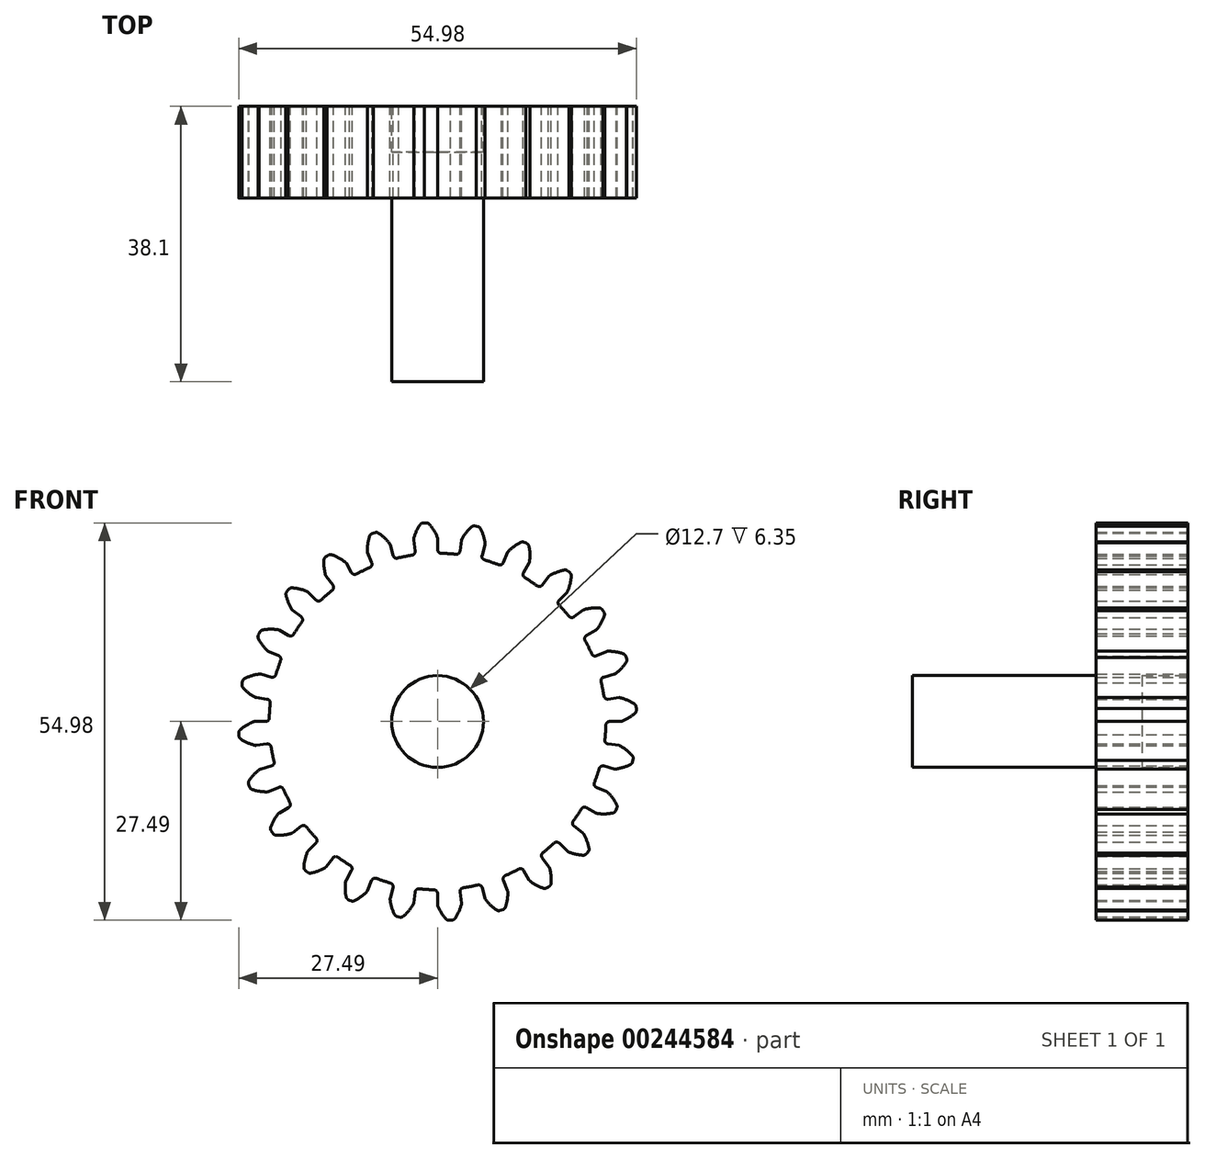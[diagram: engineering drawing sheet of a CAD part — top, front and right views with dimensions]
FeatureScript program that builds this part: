
annotation { "Feature Type Name" : "Feature", "Feature Type Description" : "" }
export const myFeature = defineFeature(function(context is Context, id is Id, definition is map)
    precondition{}
    {
        {
            var Q0;
            Q0=qCreatedBy(makeId("Front.planeOp"),FACE);
            var sketch = newSketch(context, id + "F0", { "sketchPlane" : qUnion([Q0])});
            skArc(sketch, "E0", {"start": v(-3.53, 23) * mm, "mid": v(-4.54, 22.83) * mm, "end": v(-5.54, 22.6) * mm});
            skArc(sketch, "E1.trimOffspring", {"start": v(-0.04, 25.5) * mm, "mid": v(-0.52, 26.45) * mm, "end": v(-1.16, 27.32) * mm});
            skLineSegment(sketch, "E2", {"start": v(0, 25.4) * mm, "end": v(0, 23.78) * mm});
            skLineSegment(sketch, "E3", {"start": v(-1.54, 27.49) * mm, "end": v(-1.8, 27.49) * mm});
            skLineSegment(sketch, "E4", {"start": v(0, 25.3) * mm, "end": v(0, 23.78) * mm});
            skArc(sketch, "E5.MirrorCS", {"start": v(-3.3, 25.28) * mm, "mid": v(-2.94, 26.3) * mm, "end": v(-2.41, 27.23) * mm});
            skLineSegment(sketch, "E6.MirrorCS", {"start": v(-2.06, 27.46) * mm, "end": v(-1.8, 27.49) * mm});
            skLineSegment(sketch, "E7.MirrorCS", {"start": v(-3.3, 25.09) * mm, "end": v(-3.1, 23.58) * mm});
            skPoint(sketch, "E8.visualSharp", {"position": v(-3.04, 23.08) * mm});
            skArc(sketch, "E8.filletArc", {"start": v(-3.53, 23) * mm, "mid": v(-3.2, 23.2) * mm, "end": v(-3.1, 23.58) * mm});
            skPoint(sketch, "E9.visualSharp", {"position": v(0, 23.28) * mm});
            skArc(sketch, "E9.filletArc", {"start": v(0, 23.78) * mm, "mid": v(0.14, 23.43) * mm, "end": v(0.5, 23.27) * mm});
            skPoint(sketch, "E10.visualSharp", {"position": v(0, 25.4) * mm});
            skArc(sketch, "E10.filletArc", {"start": v(0, 25.3) * mm, "mid": v(0, 25.4) * mm, "end": v(-0.04, 25.5) * mm});
            skPoint(sketch, "E11.visualSharp", {"position": v(-3.32, 25.18) * mm});
            skArc(sketch, "E11.filletArc", {"start": v(-3.3, 25.28) * mm, "mid": v(-3.3, 25.18) * mm, "end": v(-3.3, 25.09) * mm});
            skPoint(sketch, "E12.visualSharp", {"position": v(-2.28, 27.43) * mm});
            skArc(sketch, "E12.filletArc", {"start": v(-2.06, 27.46) * mm, "mid": v(-2.26, 27.38) * mm, "end": v(-2.41, 27.23) * mm});
            skPoint(sketch, "E13.visualSharp", {"position": v(-1.32, 27.49) * mm});
            skArc(sketch, "E13.filletArc", {"start": v(-1.16, 27.32) * mm, "mid": v(-1.33, 27.44) * mm, "end": v(-1.54, 27.49) * mm});
            skArc(sketch, "E14.1.0", {"start": v(-9.37, 21.31) * mm, "mid": v(-9.1, 21.59) * mm, "end": v(-9.1, 21.97) * mm});
            skLineSegment(sketch, "E14.1.1", {"start": v(-9.68, 23.38) * mm, "end": v(-9.1, 21.97) * mm});
            skArc(sketch, "E14.1.2", {"start": v(-9.72, 23.57) * mm, "mid": v(-9.71, 23.47) * mm, "end": v(-9.68, 23.38) * mm});
            skArc(sketch, "E14.1.3", {"start": v(-6.55, 24.44) * mm, "mid": v(-6.58, 24.53) * mm, "end": v(-6.63, 24.62) * mm});
            skLineSegment(sketch, "E14.1.4", {"start": v(-6.55, 24.44) * mm, "end": v(-6.16, 22.97) * mm});
            skArc(sketch, "E14.1.5", {"start": v(-6.16, 22.97) * mm, "mid": v(-5.92, 22.67) * mm, "end": v(-5.54, 22.6) * mm});
            skArc(sketch, "E14.1.6", {"start": v(-6.63, 24.62) * mm, "mid": v(-7.35, 25.42) * mm, "end": v(-8.2, 26.09) * mm});
            skArc(sketch, "E14.1.7", {"start": v(-9.72, 23.57) * mm, "mid": v(-9.64, 24.64) * mm, "end": v(-9.38, 25.68) * mm});
            skArc(sketch, "E14.1.8", {"start": v(-9.1, 25.99) * mm, "mid": v(-9.27, 25.87) * mm, "end": v(-9.38, 25.68) * mm});
            skLineSegment(sketch, "E14.1.9", {"start": v(-9.1, 25.99) * mm, "end": v(-8.86, 26.09) * mm});
            skLineSegment(sketch, "E14.1.10", {"start": v(-8.6, 26.15) * mm, "end": v(-8.86, 26.09) * mm});
            skArc(sketch, "E14.1.11", {"start": v(-8.2, 26.09) * mm, "mid": v(-8.4, 26.16) * mm, "end": v(-8.6, 26.15) * mm});
            skArc(sketch, "E14.2.0", {"start": v(-14.56, 18.16) * mm, "mid": v(-14.38, 18.5) * mm, "end": v(-14.48, 18.87) * mm});
            skLineSegment(sketch, "E14.2.1", {"start": v(-15.4, 20.07) * mm, "end": v(-14.48, 18.87) * mm});
            skArc(sketch, "E14.2.2", {"start": v(-15.5, 20.25) * mm, "mid": v(-15.46, 20.16) * mm, "end": v(-15.4, 20.07) * mm});
            skArc(sketch, "E14.2.3", {"start": v(-12.65, 21.91) * mm, "mid": v(-12.7, 22) * mm, "end": v(-12.78, 22.06) * mm});
            skLineSegment(sketch, "E14.2.4", {"start": v(-12.65, 21.91) * mm, "end": v(-11.9, 20.6) * mm});
            skArc(sketch, "E14.2.5", {"start": v(-11.9, 20.6) * mm, "mid": v(-11.59, 20.36) * mm, "end": v(-11.2, 20.4) * mm});
            skArc(sketch, "E14.2.6", {"start": v(-12.78, 22.06) * mm, "mid": v(-13.68, 22.65) * mm, "end": v(-14.66, 23.08) * mm});
            skArc(sketch, "E14.2.7", {"start": v(-15.5, 20.25) * mm, "mid": v(-15.69, 21.3) * mm, "end": v(-15.7, 22.38) * mm});
            skArc(sketch, "E14.2.8", {"start": v(-15.51, 22.75) * mm, "mid": v(-15.65, 22.58) * mm, "end": v(-15.7, 22.38) * mm});
            skLineSegment(sketch, "E14.2.9", {"start": v(-15.51, 22.75) * mm, "end": v(-15.3, 22.9) * mm});
            skLineSegment(sketch, "E14.2.10", {"start": v(-15.08, 23.04) * mm, "end": v(-15.3, 22.9) * mm});
            skArc(sketch, "E14.2.11", {"start": v(-14.66, 23.08) * mm, "mid": v(-14.88, 23.1) * mm, "end": v(-15.08, 23.04) * mm});
            skArc(sketch, "E14.3.0", {"start": v(-18.77, 13.77) * mm, "mid": v(-18.67, 14.15) * mm, "end": v(-18.87, 14.48) * mm});
            skLineSegment(sketch, "E14.3.1", {"start": v(-20.07, 15.4) * mm, "end": v(-18.87, 14.48) * mm});
            skArc(sketch, "E14.3.2", {"start": v(-20.2, 15.55) * mm, "mid": v(-20.15, 15.47) * mm, "end": v(-20.07, 15.4) * mm});
            skArc(sketch, "E14.3.3", {"start": v(-17.9, 17.9) * mm, "mid": v(-17.97, 17.95) * mm, "end": v(-18.05, 18) * mm});
            skLineSegment(sketch, "E14.3.4", {"start": v(-17.9, 17.9) * mm, "end": v(-16.82, 16.82) * mm});
            skArc(sketch, "E14.3.5", {"start": v(-16.82, 16.82) * mm, "mid": v(-16.46, 16.67) * mm, "end": v(-16.1, 16.8) * mm});
            skArc(sketch, "E14.3.6", {"start": v(-18.05, 18) * mm, "mid": v(-19.07, 18.34) * mm, "end": v(-20.14, 18.5) * mm});
            skArc(sketch, "E14.3.7", {"start": v(-20.2, 15.55) * mm, "mid": v(-20.67, 16.52) * mm, "end": v(-20.97, 17.55) * mm});
            skArc(sketch, "E14.3.8", {"start": v(-20.87, 17.96) * mm, "mid": v(-20.96, 17.76) * mm, "end": v(-20.97, 17.55) * mm});
            skLineSegment(sketch, "E14.3.9", {"start": v(-20.87, 17.96) * mm, "end": v(-20.71, 18.16) * mm});
            skLineSegment(sketch, "E14.3.10", {"start": v(-20.53, 18.35) * mm, "end": v(-20.71, 18.16) * mm});
            skArc(sketch, "E14.3.11", {"start": v(-20.14, 18.5) * mm, "mid": v(-20.35, 18.46) * mm, "end": v(-20.53, 18.35) * mm});
            skArc(sketch, "E14.4.0", {"start": v(-21.7, 8.45) * mm, "mid": v(-21.7, 8.83) * mm, "end": v(-21.97, 9.1) * mm});
            skLineSegment(sketch, "E14.4.1", {"start": v(-23.38, 9.68) * mm, "end": v(-21.97, 9.1) * mm});
            skArc(sketch, "E14.4.2", {"start": v(-23.54, 9.79) * mm, "mid": v(-23.46, 9.73) * mm, "end": v(-23.38, 9.68) * mm});
            skArc(sketch, "E14.4.3", {"start": v(-21.91, 12.65) * mm, "mid": v(-22, 12.7) * mm, "end": v(-22.1, 12.71) * mm});
            skLineSegment(sketch, "E14.4.4", {"start": v(-21.91, 12.65) * mm, "end": v(-20.6, 11.9) * mm});
            skArc(sketch, "E14.4.5", {"start": v(-20.6, 11.9) * mm, "mid": v(-20.22, 11.84) * mm, "end": v(-19.9, 12.07) * mm});
            skArc(sketch, "E14.4.6", {"start": v(-22.1, 12.71) * mm, "mid": v(-23.17, 12.77) * mm, "end": v(-24.24, 12.65) * mm});
            skArc(sketch, "E14.4.7", {"start": v(-23.54, 9.79) * mm, "mid": v(-24.24, 10.6) * mm, "end": v(-24.8, 11.53) * mm});
            skArc(sketch, "E14.4.8", {"start": v(-24.8, 11.94) * mm, "mid": v(-24.85, 11.73) * mm, "end": v(-24.8, 11.53) * mm});
            skLineSegment(sketch, "E14.4.9", {"start": v(-24.8, 11.94) * mm, "end": v(-24.7, 12.18) * mm});
            skLineSegment(sketch, "E14.4.10", {"start": v(-24.58, 12.4) * mm, "end": v(-24.7, 12.18) * mm});
            skArc(sketch, "E14.4.11", {"start": v(-24.24, 12.65) * mm, "mid": v(-24.43, 12.57) * mm, "end": v(-24.58, 12.4) * mm});
            skArc(sketch, "E14.5.0", {"start": v(-23.14, 2.54) * mm, "mid": v(-23.24, 2.91) * mm, "end": v(-23.58, 3.1) * mm});
            skLineSegment(sketch, "E14.5.1", {"start": v(-25.09, 3.3) * mm, "end": v(-23.58, 3.1) * mm});
            skArc(sketch, "E14.5.2", {"start": v(-25.27, 3.36) * mm, "mid": v(-25.18, 3.32) * mm, "end": v(-25.09, 3.3) * mm});
            skArc(sketch, "E14.5.3", {"start": v(-24.44, 6.55) * mm, "mid": v(-24.54, 6.57) * mm, "end": v(-24.63, 6.56) * mm});
            skLineSegment(sketch, "E14.5.4", {"start": v(-24.44, 6.55) * mm, "end": v(-22.97, 6.16) * mm});
            skArc(sketch, "E14.5.5", {"start": v(-22.97, 6.16) * mm, "mid": v(-22.6, 6.2) * mm, "end": v(-22.35, 6.5) * mm});
            skArc(sketch, "E14.5.6", {"start": v(-24.63, 6.56) * mm, "mid": v(-25.69, 6.34) * mm, "end": v(-26.69, 5.95) * mm});
            skArc(sketch, "E14.5.7", {"start": v(-25.27, 3.36) * mm, "mid": v(-26.16, 3.97) * mm, "end": v(-26.93, 4.72) * mm});
            skArc(sketch, "E14.5.8", {"start": v(-27.05, 5.12) * mm, "mid": v(-27.04, 4.9) * mm, "end": v(-26.93, 4.72) * mm});
            skLineSegment(sketch, "E14.5.9", {"start": v(-27.05, 5.12) * mm, "end": v(-27.02, 5.37) * mm});
            skLineSegment(sketch, "E14.5.10", {"start": v(-26.95, 5.63) * mm, "end": v(-27.02, 5.37) * mm});
            skArc(sketch, "E14.5.11", {"start": v(-26.69, 5.95) * mm, "mid": v(-26.85, 5.82) * mm, "end": v(-26.95, 5.63) * mm});
            skArc(sketch, "E14.6.0", {"start": v(-23, -3.53) * mm, "mid": v(-23.2, -3.2) * mm, "end": v(-23.58, -3.1) * mm});
            skLineSegment(sketch, "E14.6.1", {"start": v(-25.09, -3.3) * mm, "end": v(-23.58, -3.1) * mm});
            skArc(sketch, "E14.6.2", {"start": v(-25.28, -3.3) * mm, "mid": v(-25.18, -3.3) * mm, "end": v(-25.09, -3.3) * mm});
            skArc(sketch, "E14.6.3", {"start": v(-25.3, 0) * mm, "mid": v(-25.4, 0) * mm, "end": v(-25.5, -0.04) * mm});
            skLineSegment(sketch, "E14.6.4", {"start": v(-25.3, 0) * mm, "end": v(-23.78, 0) * mm});
            skArc(sketch, "E14.6.5", {"start": v(-23.78, 0) * mm, "mid": v(-23.43, 0.14) * mm, "end": v(-23.27, 0.5) * mm});
            skArc(sketch, "E14.6.6", {"start": v(-25.5, -0.04) * mm, "mid": v(-26.45, -0.52) * mm, "end": v(-27.32, -1.16) * mm});
            skArc(sketch, "E14.6.7", {"start": v(-25.28, -3.3) * mm, "mid": v(-26.3, -2.94) * mm, "end": v(-27.23, -2.41) * mm});
            skArc(sketch, "E14.6.8", {"start": v(-27.46, -2.06) * mm, "mid": v(-27.38, -2.26) * mm, "end": v(-27.23, -2.41) * mm});
            skLineSegment(sketch, "E14.6.9", {"start": v(-27.46, -2.06) * mm, "end": v(-27.49, -1.8) * mm});
            skLineSegment(sketch, "E14.6.10", {"start": v(-27.49, -1.54) * mm, "end": v(-27.49, -1.8) * mm});
            skArc(sketch, "E14.6.11", {"start": v(-27.32, -1.16) * mm, "mid": v(-27.44, -1.33) * mm, "end": v(-27.49, -1.54) * mm});
            skArc(sketch, "E14.7.0", {"start": v(-21.31, -9.37) * mm, "mid": v(-21.59, -9.1) * mm, "end": v(-21.97, -9.1) * mm});
            skLineSegment(sketch, "E14.7.1", {"start": v(-23.38, -9.68) * mm, "end": v(-21.97, -9.1) * mm});
            skArc(sketch, "E14.7.2", {"start": v(-23.57, -9.72) * mm, "mid": v(-23.47, -9.71) * mm, "end": v(-23.38, -9.68) * mm});
            skArc(sketch, "E14.7.3", {"start": v(-24.44, -6.55) * mm, "mid": v(-24.53, -6.58) * mm, "end": v(-24.62, -6.63) * mm});
            skLineSegment(sketch, "E14.7.4", {"start": v(-24.44, -6.55) * mm, "end": v(-22.97, -6.16) * mm});
            skArc(sketch, "E14.7.5", {"start": v(-22.97, -6.16) * mm, "mid": v(-22.67, -5.92) * mm, "end": v(-22.6, -5.54) * mm});
            skArc(sketch, "E14.7.6", {"start": v(-24.62, -6.63) * mm, "mid": v(-25.42, -7.35) * mm, "end": v(-26.09, -8.2) * mm});
            skArc(sketch, "E14.7.7", {"start": v(-23.57, -9.72) * mm, "mid": v(-24.64, -9.64) * mm, "end": v(-25.68, -9.38) * mm});
            skArc(sketch, "E14.7.8", {"start": v(-25.99, -9.1) * mm, "mid": v(-25.87, -9.27) * mm, "end": v(-25.68, -9.38) * mm});
            skLineSegment(sketch, "E14.7.9", {"start": v(-25.99, -9.1) * mm, "end": v(-26.09, -8.86) * mm});
            skLineSegment(sketch, "E14.7.10", {"start": v(-26.15, -8.6) * mm, "end": v(-26.09, -8.86) * mm});
            skArc(sketch, "E14.7.11", {"start": v(-26.09, -8.2) * mm, "mid": v(-26.16, -8.4) * mm, "end": v(-26.15, -8.6) * mm});
            skArc(sketch, "E14.8.0", {"start": v(-18.16, -14.56) * mm, "mid": v(-18.5, -14.38) * mm, "end": v(-18.87, -14.48) * mm});
            skLineSegment(sketch, "E14.8.1", {"start": v(-20.07, -15.4) * mm, "end": v(-18.87, -14.48) * mm});
            skArc(sketch, "E14.8.2", {"start": v(-20.25, -15.5) * mm, "mid": v(-20.16, -15.46) * mm, "end": v(-20.07, -15.4) * mm});
            skArc(sketch, "E14.8.3", {"start": v(-21.91, -12.65) * mm, "mid": v(-22, -12.7) * mm, "end": v(-22.06, -12.78) * mm});
            skLineSegment(sketch, "E14.8.4", {"start": v(-21.91, -12.65) * mm, "end": v(-20.6, -11.9) * mm});
            skArc(sketch, "E14.8.5", {"start": v(-20.6, -11.9) * mm, "mid": v(-20.36, -11.59) * mm, "end": v(-20.4, -11.2) * mm});
            skArc(sketch, "E14.8.6", {"start": v(-22.06, -12.78) * mm, "mid": v(-22.65, -13.68) * mm, "end": v(-23.08, -14.66) * mm});
            skArc(sketch, "E14.8.7", {"start": v(-20.25, -15.5) * mm, "mid": v(-21.3, -15.69) * mm, "end": v(-22.38, -15.7) * mm});
            skArc(sketch, "E14.8.8", {"start": v(-22.75, -15.51) * mm, "mid": v(-22.58, -15.65) * mm, "end": v(-22.38, -15.7) * mm});
            skLineSegment(sketch, "E14.8.9", {"start": v(-22.75, -15.51) * mm, "end": v(-22.9, -15.3) * mm});
            skLineSegment(sketch, "E14.8.10", {"start": v(-23.04, -15.08) * mm, "end": v(-22.9, -15.3) * mm});
            skArc(sketch, "E14.8.11", {"start": v(-23.08, -14.66) * mm, "mid": v(-23.1, -14.88) * mm, "end": v(-23.04, -15.08) * mm});
            skArc(sketch, "E14.9.0", {"start": v(-13.77, -18.77) * mm, "mid": v(-14.15, -18.67) * mm, "end": v(-14.48, -18.87) * mm});
            skLineSegment(sketch, "E14.9.1", {"start": v(-15.4, -20.07) * mm, "end": v(-14.48, -18.87) * mm});
            skArc(sketch, "E14.9.2", {"start": v(-15.55, -20.2) * mm, "mid": v(-15.47, -20.15) * mm, "end": v(-15.4, -20.07) * mm});
            skArc(sketch, "E14.9.3", {"start": v(-17.9, -17.9) * mm, "mid": v(-17.95, -17.97) * mm, "end": v(-18, -18.05) * mm});
            skLineSegment(sketch, "E14.9.4", {"start": v(-17.9, -17.9) * mm, "end": v(-16.82, -16.82) * mm});
            skArc(sketch, "E14.9.5", {"start": v(-16.82, -16.82) * mm, "mid": v(-16.67, -16.46) * mm, "end": v(-16.8, -16.1) * mm});
            skArc(sketch, "E14.9.6", {"start": v(-18, -18.05) * mm, "mid": v(-18.34, -19.07) * mm, "end": v(-18.5, -20.14) * mm});
            skArc(sketch, "E14.9.7", {"start": v(-15.55, -20.2) * mm, "mid": v(-16.52, -20.67) * mm, "end": v(-17.55, -20.97) * mm});
            skArc(sketch, "E14.9.8", {"start": v(-17.96, -20.87) * mm, "mid": v(-17.76, -20.96) * mm, "end": v(-17.55, -20.97) * mm});
            skLineSegment(sketch, "E14.9.9", {"start": v(-17.96, -20.87) * mm, "end": v(-18.16, -20.71) * mm});
            skLineSegment(sketch, "E14.9.10", {"start": v(-18.35, -20.53) * mm, "end": v(-18.16, -20.71) * mm});
            skArc(sketch, "E14.9.11", {"start": v(-18.5, -20.14) * mm, "mid": v(-18.46, -20.35) * mm, "end": v(-18.35, -20.53) * mm});
            skArc(sketch, "E14.10.0", {"start": v(-8.45, -21.7) * mm, "mid": v(-8.83, -21.7) * mm, "end": v(-9.1, -21.97) * mm});
            skLineSegment(sketch, "E14.10.1", {"start": v(-9.68, -23.38) * mm, "end": v(-9.1, -21.97) * mm});
            skArc(sketch, "E14.10.2", {"start": v(-9.79, -23.54) * mm, "mid": v(-9.73, -23.46) * mm, "end": v(-9.68, -23.38) * mm});
            skArc(sketch, "E14.10.3", {"start": v(-12.65, -21.91) * mm, "mid": v(-12.7, -22) * mm, "end": v(-12.71, -22.1) * mm});
            skLineSegment(sketch, "E14.10.4", {"start": v(-12.65, -21.91) * mm, "end": v(-11.9, -20.6) * mm});
            skArc(sketch, "E14.10.5", {"start": v(-11.9, -20.6) * mm, "mid": v(-11.84, -20.22) * mm, "end": v(-12.07, -19.9) * mm});
            skArc(sketch, "E14.10.6", {"start": v(-12.71, -22.1) * mm, "mid": v(-12.77, -23.17) * mm, "end": v(-12.65, -24.24) * mm});
            skArc(sketch, "E14.10.7", {"start": v(-9.79, -23.54) * mm, "mid": v(-10.6, -24.24) * mm, "end": v(-11.53, -24.8) * mm});
            skArc(sketch, "E14.10.8", {"start": v(-11.94, -24.8) * mm, "mid": v(-11.73, -24.85) * mm, "end": v(-11.53, -24.8) * mm});
            skLineSegment(sketch, "E14.10.9", {"start": v(-11.94, -24.8) * mm, "end": v(-12.18, -24.7) * mm});
            skLineSegment(sketch, "E14.10.10", {"start": v(-12.4, -24.58) * mm, "end": v(-12.18, -24.7) * mm});
            skArc(sketch, "E14.10.11", {"start": v(-12.65, -24.24) * mm, "mid": v(-12.57, -24.43) * mm, "end": v(-12.4, -24.58) * mm});
            skArc(sketch, "E14.11.0", {"start": v(-2.54, -23.14) * mm, "mid": v(-2.91, -23.24) * mm, "end": v(-3.1, -23.58) * mm});
            skLineSegment(sketch, "E14.11.1", {"start": v(-3.3, -25.09) * mm, "end": v(-3.1, -23.58) * mm});
            skArc(sketch, "E14.11.2", {"start": v(-3.36, -25.27) * mm, "mid": v(-3.32, -25.18) * mm, "end": v(-3.3, -25.09) * mm});
            skArc(sketch, "E14.11.3", {"start": v(-6.55, -24.44) * mm, "mid": v(-6.57, -24.54) * mm, "end": v(-6.56, -24.63) * mm});
            skLineSegment(sketch, "E14.11.4", {"start": v(-6.55, -24.44) * mm, "end": v(-6.16, -22.97) * mm});
            skArc(sketch, "E14.11.5", {"start": v(-6.16, -22.97) * mm, "mid": v(-6.2, -22.6) * mm, "end": v(-6.5, -22.35) * mm});
            skArc(sketch, "E14.11.6", {"start": v(-6.56, -24.63) * mm, "mid": v(-6.34, -25.69) * mm, "end": v(-5.95, -26.69) * mm});
            skArc(sketch, "E14.11.7", {"start": v(-3.36, -25.27) * mm, "mid": v(-3.97, -26.16) * mm, "end": v(-4.72, -26.93) * mm});
            skArc(sketch, "E14.11.8", {"start": v(-5.12, -27.05) * mm, "mid": v(-4.9, -27.04) * mm, "end": v(-4.72, -26.93) * mm});
            skLineSegment(sketch, "E14.11.9", {"start": v(-5.12, -27.05) * mm, "end": v(-5.37, -27.02) * mm});
            skLineSegment(sketch, "E14.11.10", {"start": v(-5.63, -26.95) * mm, "end": v(-5.37, -27.02) * mm});
            skArc(sketch, "E14.11.11", {"start": v(-5.95, -26.69) * mm, "mid": v(-5.82, -26.85) * mm, "end": v(-5.63, -26.95) * mm});
            skArc(sketch, "E14.12.0", {"start": v(3.53, -23) * mm, "mid": v(3.2, -23.2) * mm, "end": v(3.1, -23.58) * mm});
            skLineSegment(sketch, "E14.12.1", {"start": v(3.3, -25.09) * mm, "end": v(3.1, -23.58) * mm});
            skArc(sketch, "E14.12.2", {"start": v(3.3, -25.28) * mm, "mid": v(3.3, -25.18) * mm, "end": v(3.3, -25.09) * mm});
            skArc(sketch, "E14.12.3", {"start": v(0, -25.3) * mm, "mid": v(0, -25.4) * mm, "end": v(0.04, -25.5) * mm});
            skLineSegment(sketch, "E14.12.4", {"start": v(0, -25.3) * mm, "end": v(0, -23.78) * mm});
            skArc(sketch, "E14.12.5", {"start": v(0, -23.78) * mm, "mid": v(-0.14, -23.43) * mm, "end": v(-0.5, -23.27) * mm});
            skArc(sketch, "E14.12.6", {"start": v(0.04, -25.5) * mm, "mid": v(0.52, -26.45) * mm, "end": v(1.16, -27.32) * mm});
            skArc(sketch, "E14.12.7", {"start": v(3.3, -25.28) * mm, "mid": v(2.94, -26.3) * mm, "end": v(2.41, -27.23) * mm});
            skArc(sketch, "E14.12.8", {"start": v(2.06, -27.46) * mm, "mid": v(2.26, -27.38) * mm, "end": v(2.41, -27.23) * mm});
            skLineSegment(sketch, "E14.12.9", {"start": v(2.06, -27.46) * mm, "end": v(1.8, -27.49) * mm});
            skLineSegment(sketch, "E14.12.10", {"start": v(1.54, -27.49) * mm, "end": v(1.8, -27.49) * mm});
            skArc(sketch, "E14.12.11", {"start": v(1.16, -27.32) * mm, "mid": v(1.33, -27.44) * mm, "end": v(1.54, -27.49) * mm});
            skArc(sketch, "E14.13.0", {"start": v(9.37, -21.31) * mm, "mid": v(9.1, -21.59) * mm, "end": v(9.1, -21.97) * mm});
            skLineSegment(sketch, "E14.13.1", {"start": v(9.68, -23.38) * mm, "end": v(9.1, -21.97) * mm});
            skArc(sketch, "E14.13.2", {"start": v(9.72, -23.57) * mm, "mid": v(9.71, -23.47) * mm, "end": v(9.68, -23.38) * mm});
            skArc(sketch, "E14.13.3", {"start": v(6.55, -24.44) * mm, "mid": v(6.58, -24.53) * mm, "end": v(6.63, -24.62) * mm});
            skLineSegment(sketch, "E14.13.4", {"start": v(6.55, -24.44) * mm, "end": v(6.16, -22.97) * mm});
            skArc(sketch, "E14.13.5", {"start": v(6.16, -22.97) * mm, "mid": v(5.92, -22.67) * mm, "end": v(5.54, -22.6) * mm});
            skArc(sketch, "E14.13.6", {"start": v(6.63, -24.62) * mm, "mid": v(7.35, -25.42) * mm, "end": v(8.2, -26.09) * mm});
            skArc(sketch, "E14.13.7", {"start": v(9.72, -23.57) * mm, "mid": v(9.64, -24.64) * mm, "end": v(9.38, -25.68) * mm});
            skArc(sketch, "E14.13.8", {"start": v(9.1, -25.99) * mm, "mid": v(9.27, -25.87) * mm, "end": v(9.38, -25.68) * mm});
            skLineSegment(sketch, "E14.13.9", {"start": v(9.1, -25.99) * mm, "end": v(8.86, -26.09) * mm});
            skLineSegment(sketch, "E14.13.10", {"start": v(8.6, -26.15) * mm, "end": v(8.86, -26.09) * mm});
            skArc(sketch, "E14.13.11", {"start": v(8.2, -26.09) * mm, "mid": v(8.4, -26.16) * mm, "end": v(8.6, -26.15) * mm});
            skArc(sketch, "E14.14.0", {"start": v(14.56, -18.16) * mm, "mid": v(14.38, -18.5) * mm, "end": v(14.48, -18.87) * mm});
            skLineSegment(sketch, "E14.14.1", {"start": v(15.4, -20.07) * mm, "end": v(14.48, -18.87) * mm});
            skArc(sketch, "E14.14.2", {"start": v(15.5, -20.25) * mm, "mid": v(15.46, -20.16) * mm, "end": v(15.4, -20.07) * mm});
            skArc(sketch, "E14.14.3", {"start": v(12.65, -21.91) * mm, "mid": v(12.7, -22) * mm, "end": v(12.78, -22.06) * mm});
            skLineSegment(sketch, "E14.14.4", {"start": v(12.65, -21.91) * mm, "end": v(11.9, -20.6) * mm});
            skArc(sketch, "E14.14.5", {"start": v(11.9, -20.6) * mm, "mid": v(11.59, -20.36) * mm, "end": v(11.2, -20.4) * mm});
            skArc(sketch, "E14.14.6", {"start": v(12.78, -22.06) * mm, "mid": v(13.68, -22.65) * mm, "end": v(14.66, -23.08) * mm});
            skArc(sketch, "E14.14.7", {"start": v(15.5, -20.25) * mm, "mid": v(15.69, -21.3) * mm, "end": v(15.7, -22.38) * mm});
            skArc(sketch, "E14.14.8", {"start": v(15.51, -22.75) * mm, "mid": v(15.65, -22.58) * mm, "end": v(15.7, -22.38) * mm});
            skLineSegment(sketch, "E14.14.9", {"start": v(15.51, -22.75) * mm, "end": v(15.3, -22.9) * mm});
            skLineSegment(sketch, "E14.14.10", {"start": v(15.08, -23.04) * mm, "end": v(15.3, -22.9) * mm});
            skArc(sketch, "E14.14.11", {"start": v(14.66, -23.08) * mm, "mid": v(14.88, -23.1) * mm, "end": v(15.08, -23.04) * mm});
            skArc(sketch, "E14.15.0", {"start": v(18.77, -13.77) * mm, "mid": v(18.67, -14.15) * mm, "end": v(18.87, -14.48) * mm});
            skLineSegment(sketch, "E14.15.1", {"start": v(20.07, -15.4) * mm, "end": v(18.87, -14.48) * mm});
            skArc(sketch, "E14.15.2", {"start": v(20.2, -15.55) * mm, "mid": v(20.15, -15.47) * mm, "end": v(20.07, -15.4) * mm});
            skArc(sketch, "E14.15.3", {"start": v(17.9, -17.9) * mm, "mid": v(17.97, -17.95) * mm, "end": v(18.05, -18) * mm});
            skLineSegment(sketch, "E14.15.4", {"start": v(17.9, -17.9) * mm, "end": v(16.82, -16.82) * mm});
            skArc(sketch, "E14.15.5", {"start": v(16.82, -16.82) * mm, "mid": v(16.46, -16.67) * mm, "end": v(16.1, -16.8) * mm});
            skArc(sketch, "E14.15.6", {"start": v(18.05, -18) * mm, "mid": v(19.07, -18.34) * mm, "end": v(20.14, -18.5) * mm});
            skArc(sketch, "E14.15.7", {"start": v(20.2, -15.55) * mm, "mid": v(20.67, -16.52) * mm, "end": v(20.97, -17.55) * mm});
            skArc(sketch, "E14.15.8", {"start": v(20.87, -17.96) * mm, "mid": v(20.96, -17.76) * mm, "end": v(20.97, -17.55) * mm});
            skLineSegment(sketch, "E14.15.9", {"start": v(20.87, -17.96) * mm, "end": v(20.71, -18.16) * mm});
            skLineSegment(sketch, "E14.15.10", {"start": v(20.53, -18.35) * mm, "end": v(20.71, -18.16) * mm});
            skArc(sketch, "E14.15.11", {"start": v(20.14, -18.5) * mm, "mid": v(20.35, -18.46) * mm, "end": v(20.53, -18.35) * mm});
            skArc(sketch, "E14.16.0", {"start": v(21.7, -8.45) * mm, "mid": v(21.7, -8.83) * mm, "end": v(21.97, -9.1) * mm});
            skLineSegment(sketch, "E14.16.1", {"start": v(23.38, -9.68) * mm, "end": v(21.97, -9.1) * mm});
            skArc(sketch, "E14.16.2", {"start": v(23.54, -9.79) * mm, "mid": v(23.46, -9.73) * mm, "end": v(23.38, -9.68) * mm});
            skArc(sketch, "E14.16.3", {"start": v(21.91, -12.65) * mm, "mid": v(22, -12.7) * mm, "end": v(22.1, -12.71) * mm});
            skLineSegment(sketch, "E14.16.4", {"start": v(21.91, -12.65) * mm, "end": v(20.6, -11.9) * mm});
            skArc(sketch, "E14.16.5", {"start": v(20.6, -11.9) * mm, "mid": v(20.22, -11.84) * mm, "end": v(19.9, -12.07) * mm});
            skArc(sketch, "E14.16.6", {"start": v(22.1, -12.71) * mm, "mid": v(23.17, -12.77) * mm, "end": v(24.24, -12.65) * mm});
            skArc(sketch, "E14.16.7", {"start": v(23.54, -9.79) * mm, "mid": v(24.24, -10.6) * mm, "end": v(24.8, -11.53) * mm});
            skArc(sketch, "E14.16.8", {"start": v(24.8, -11.94) * mm, "mid": v(24.85, -11.73) * mm, "end": v(24.8, -11.53) * mm});
            skLineSegment(sketch, "E14.16.9", {"start": v(24.8, -11.94) * mm, "end": v(24.7, -12.18) * mm});
            skLineSegment(sketch, "E14.16.10", {"start": v(24.58, -12.4) * mm, "end": v(24.7, -12.18) * mm});
            skArc(sketch, "E14.16.11", {"start": v(24.24, -12.65) * mm, "mid": v(24.43, -12.57) * mm, "end": v(24.58, -12.4) * mm});
            skArc(sketch, "E14.17.0", {"start": v(23.14, -2.54) * mm, "mid": v(23.24, -2.91) * mm, "end": v(23.58, -3.1) * mm});
            skLineSegment(sketch, "E14.17.1", {"start": v(25.09, -3.3) * mm, "end": v(23.58, -3.1) * mm});
            skArc(sketch, "E14.17.2", {"start": v(25.27, -3.36) * mm, "mid": v(25.18, -3.32) * mm, "end": v(25.09, -3.3) * mm});
            skArc(sketch, "E14.17.3", {"start": v(24.44, -6.55) * mm, "mid": v(24.54, -6.57) * mm, "end": v(24.63, -6.56) * mm});
            skLineSegment(sketch, "E14.17.4", {"start": v(24.44, -6.55) * mm, "end": v(22.97, -6.16) * mm});
            skArc(sketch, "E14.17.5", {"start": v(22.97, -6.16) * mm, "mid": v(22.6, -6.2) * mm, "end": v(22.35, -6.5) * mm});
            skArc(sketch, "E14.17.6", {"start": v(24.63, -6.56) * mm, "mid": v(25.69, -6.34) * mm, "end": v(26.69, -5.95) * mm});
            skArc(sketch, "E14.17.7", {"start": v(25.27, -3.36) * mm, "mid": v(26.16, -3.97) * mm, "end": v(26.93, -4.72) * mm});
            skArc(sketch, "E14.17.8", {"start": v(27.05, -5.12) * mm, "mid": v(27.04, -4.9) * mm, "end": v(26.93, -4.72) * mm});
            skLineSegment(sketch, "E14.17.9", {"start": v(27.05, -5.12) * mm, "end": v(27.02, -5.37) * mm});
            skLineSegment(sketch, "E14.17.10", {"start": v(26.95, -5.63) * mm, "end": v(27.02, -5.37) * mm});
            skArc(sketch, "E14.17.11", {"start": v(26.69, -5.95) * mm, "mid": v(26.85, -5.82) * mm, "end": v(26.95, -5.63) * mm});
            skArc(sketch, "E14.18.0", {"start": v(23, 3.53) * mm, "mid": v(23.2, 3.2) * mm, "end": v(23.58, 3.1) * mm});
            skLineSegment(sketch, "E14.18.1", {"start": v(25.09, 3.3) * mm, "end": v(23.58, 3.1) * mm});
            skArc(sketch, "E14.18.2", {"start": v(25.28, 3.3) * mm, "mid": v(25.18, 3.3) * mm, "end": v(25.09, 3.3) * mm});
            skArc(sketch, "E14.18.3", {"start": v(25.3, 0) * mm, "mid": v(25.4, 0) * mm, "end": v(25.5, 0.04) * mm});
            skLineSegment(sketch, "E14.18.4", {"start": v(25.3, 0) * mm, "end": v(23.78, 0) * mm});
            skArc(sketch, "E14.18.5", {"start": v(23.78, 0) * mm, "mid": v(23.43, -0.14) * mm, "end": v(23.27, -0.5) * mm});
            skArc(sketch, "E14.18.6", {"start": v(25.5, 0.04) * mm, "mid": v(26.45, 0.52) * mm, "end": v(27.32, 1.16) * mm});
            skArc(sketch, "E14.18.7", {"start": v(25.28, 3.3) * mm, "mid": v(26.3, 2.94) * mm, "end": v(27.23, 2.41) * mm});
            skArc(sketch, "E14.18.8", {"start": v(27.46, 2.06) * mm, "mid": v(27.38, 2.26) * mm, "end": v(27.23, 2.41) * mm});
            skLineSegment(sketch, "E14.18.9", {"start": v(27.46, 2.06) * mm, "end": v(27.49, 1.8) * mm});
            skLineSegment(sketch, "E14.18.10", {"start": v(27.49, 1.54) * mm, "end": v(27.49, 1.8) * mm});
            skArc(sketch, "E14.18.11", {"start": v(27.32, 1.16) * mm, "mid": v(27.44, 1.33) * mm, "end": v(27.49, 1.54) * mm});
            skArc(sketch, "E14.19.0", {"start": v(21.31, 9.37) * mm, "mid": v(21.59, 9.1) * mm, "end": v(21.97, 9.1) * mm});
            skLineSegment(sketch, "E14.19.1", {"start": v(23.38, 9.68) * mm, "end": v(21.97, 9.1) * mm});
            skArc(sketch, "E14.19.2", {"start": v(23.57, 9.72) * mm, "mid": v(23.47, 9.71) * mm, "end": v(23.38, 9.68) * mm});
            skArc(sketch, "E14.19.3", {"start": v(24.44, 6.55) * mm, "mid": v(24.53, 6.58) * mm, "end": v(24.62, 6.63) * mm});
            skLineSegment(sketch, "E14.19.4", {"start": v(24.44, 6.55) * mm, "end": v(22.97, 6.16) * mm});
            skArc(sketch, "E14.19.5", {"start": v(22.97, 6.16) * mm, "mid": v(22.67, 5.92) * mm, "end": v(22.6, 5.54) * mm});
            skArc(sketch, "E14.19.6", {"start": v(24.62, 6.63) * mm, "mid": v(25.42, 7.35) * mm, "end": v(26.09, 8.2) * mm});
            skArc(sketch, "E14.19.7", {"start": v(23.57, 9.72) * mm, "mid": v(24.64, 9.64) * mm, "end": v(25.68, 9.38) * mm});
            skArc(sketch, "E14.19.8", {"start": v(25.99, 9.1) * mm, "mid": v(25.87, 9.27) * mm, "end": v(25.68, 9.38) * mm});
            skLineSegment(sketch, "E14.19.9", {"start": v(25.99, 9.1) * mm, "end": v(26.09, 8.86) * mm});
            skLineSegment(sketch, "E14.19.10", {"start": v(26.15, 8.6) * mm, "end": v(26.09, 8.86) * mm});
            skArc(sketch, "E14.19.11", {"start": v(26.09, 8.2) * mm, "mid": v(26.16, 8.4) * mm, "end": v(26.15, 8.6) * mm});
            skArc(sketch, "E14.20.0", {"start": v(18.16, 14.56) * mm, "mid": v(18.5, 14.38) * mm, "end": v(18.87, 14.48) * mm});
            skLineSegment(sketch, "E14.20.1", {"start": v(20.07, 15.4) * mm, "end": v(18.87, 14.48) * mm});
            skArc(sketch, "E14.20.2", {"start": v(20.25, 15.5) * mm, "mid": v(20.16, 15.46) * mm, "end": v(20.07, 15.4) * mm});
            skArc(sketch, "E14.20.3", {"start": v(21.91, 12.65) * mm, "mid": v(22, 12.7) * mm, "end": v(22.06, 12.78) * mm});
            skLineSegment(sketch, "E14.20.4", {"start": v(21.91, 12.65) * mm, "end": v(20.6, 11.9) * mm});
            skArc(sketch, "E14.20.5", {"start": v(20.6, 11.9) * mm, "mid": v(20.36, 11.59) * mm, "end": v(20.4, 11.2) * mm});
            skArc(sketch, "E14.20.6", {"start": v(22.06, 12.78) * mm, "mid": v(22.65, 13.68) * mm, "end": v(23.08, 14.66) * mm});
            skArc(sketch, "E14.20.7", {"start": v(20.25, 15.5) * mm, "mid": v(21.3, 15.69) * mm, "end": v(22.38, 15.7) * mm});
            skArc(sketch, "E14.20.8", {"start": v(22.75, 15.51) * mm, "mid": v(22.58, 15.65) * mm, "end": v(22.38, 15.7) * mm});
            skLineSegment(sketch, "E14.20.9", {"start": v(22.75, 15.51) * mm, "end": v(22.9, 15.3) * mm});
            skLineSegment(sketch, "E14.20.10", {"start": v(23.04, 15.08) * mm, "end": v(22.9, 15.3) * mm});
            skArc(sketch, "E14.20.11", {"start": v(23.08, 14.66) * mm, "mid": v(23.1, 14.88) * mm, "end": v(23.04, 15.08) * mm});
            skArc(sketch, "E14.21.0", {"start": v(13.77, 18.77) * mm, "mid": v(14.15, 18.67) * mm, "end": v(14.48, 18.87) * mm});
            skLineSegment(sketch, "E14.21.1", {"start": v(15.4, 20.07) * mm, "end": v(14.48, 18.87) * mm});
            skArc(sketch, "E14.21.2", {"start": v(15.55, 20.2) * mm, "mid": v(15.47, 20.15) * mm, "end": v(15.4, 20.07) * mm});
            skArc(sketch, "E14.21.3", {"start": v(17.9, 17.9) * mm, "mid": v(17.95, 17.97) * mm, "end": v(18, 18.05) * mm});
            skLineSegment(sketch, "E14.21.4", {"start": v(17.9, 17.9) * mm, "end": v(16.82, 16.82) * mm});
            skArc(sketch, "E14.21.5", {"start": v(16.82, 16.82) * mm, "mid": v(16.67, 16.46) * mm, "end": v(16.8, 16.1) * mm});
            skArc(sketch, "E14.21.6", {"start": v(18, 18.05) * mm, "mid": v(18.34, 19.07) * mm, "end": v(18.5, 20.14) * mm});
            skArc(sketch, "E14.21.7", {"start": v(15.55, 20.2) * mm, "mid": v(16.52, 20.67) * mm, "end": v(17.55, 20.97) * mm});
            skArc(sketch, "E14.21.8", {"start": v(17.96, 20.87) * mm, "mid": v(17.76, 20.96) * mm, "end": v(17.55, 20.97) * mm});
            skLineSegment(sketch, "E14.21.9", {"start": v(17.96, 20.87) * mm, "end": v(18.16, 20.71) * mm});
            skLineSegment(sketch, "E14.21.10", {"start": v(18.35, 20.53) * mm, "end": v(18.16, 20.71) * mm});
            skArc(sketch, "E14.21.11", {"start": v(18.5, 20.14) * mm, "mid": v(18.46, 20.35) * mm, "end": v(18.35, 20.53) * mm});
            skArc(sketch, "E14.22.0", {"start": v(8.45, 21.7) * mm, "mid": v(8.83, 21.7) * mm, "end": v(9.1, 21.97) * mm});
            skLineSegment(sketch, "E14.22.1", {"start": v(9.68, 23.38) * mm, "end": v(9.1, 21.97) * mm});
            skArc(sketch, "E14.22.2", {"start": v(9.79, 23.54) * mm, "mid": v(9.73, 23.46) * mm, "end": v(9.68, 23.38) * mm});
            skArc(sketch, "E14.22.3", {"start": v(12.65, 21.91) * mm, "mid": v(12.7, 22) * mm, "end": v(12.71, 22.1) * mm});
            skLineSegment(sketch, "E14.22.4", {"start": v(12.65, 21.91) * mm, "end": v(11.9, 20.6) * mm});
            skArc(sketch, "E14.22.5", {"start": v(11.9, 20.6) * mm, "mid": v(11.84, 20.22) * mm, "end": v(12.07, 19.9) * mm});
            skArc(sketch, "E14.22.6", {"start": v(12.71, 22.1) * mm, "mid": v(12.77, 23.17) * mm, "end": v(12.65, 24.24) * mm});
            skArc(sketch, "E14.22.7", {"start": v(9.79, 23.54) * mm, "mid": v(10.6, 24.24) * mm, "end": v(11.53, 24.8) * mm});
            skArc(sketch, "E14.22.8", {"start": v(11.94, 24.8) * mm, "mid": v(11.73, 24.85) * mm, "end": v(11.53, 24.8) * mm});
            skLineSegment(sketch, "E14.22.9", {"start": v(11.94, 24.8) * mm, "end": v(12.18, 24.7) * mm});
            skLineSegment(sketch, "E14.22.10", {"start": v(12.4, 24.58) * mm, "end": v(12.18, 24.7) * mm});
            skArc(sketch, "E14.22.11", {"start": v(12.65, 24.24) * mm, "mid": v(12.57, 24.43) * mm, "end": v(12.4, 24.58) * mm});
            skArc(sketch, "E14.23.0", {"start": v(2.54, 23.14) * mm, "mid": v(2.91, 23.24) * mm, "end": v(3.1, 23.58) * mm});
            skLineSegment(sketch, "E14.23.1", {"start": v(3.3, 25.09) * mm, "end": v(3.1, 23.58) * mm});
            skArc(sketch, "E14.23.2", {"start": v(3.36, 25.27) * mm, "mid": v(3.32, 25.18) * mm, "end": v(3.3, 25.09) * mm});
            skArc(sketch, "E14.23.3", {"start": v(6.55, 24.44) * mm, "mid": v(6.57, 24.54) * mm, "end": v(6.56, 24.63) * mm});
            skLineSegment(sketch, "E14.23.4", {"start": v(6.55, 24.44) * mm, "end": v(6.16, 22.97) * mm});
            skArc(sketch, "E14.23.5", {"start": v(6.16, 22.97) * mm, "mid": v(6.2, 22.6) * mm, "end": v(6.5, 22.35) * mm});
            skArc(sketch, "E14.23.6", {"start": v(6.56, 24.63) * mm, "mid": v(6.34, 25.69) * mm, "end": v(5.95, 26.69) * mm});
            skArc(sketch, "E14.23.7", {"start": v(3.36, 25.27) * mm, "mid": v(3.97, 26.16) * mm, "end": v(4.72, 26.93) * mm});
            skArc(sketch, "E14.23.8", {"start": v(5.12, 27.05) * mm, "mid": v(4.9, 27.04) * mm, "end": v(4.72, 26.93) * mm});
            skLineSegment(sketch, "E14.23.9", {"start": v(5.12, 27.05) * mm, "end": v(5.37, 27.02) * mm});
            skLineSegment(sketch, "E14.23.10", {"start": v(5.63, 26.95) * mm, "end": v(5.37, 27.02) * mm});
            skArc(sketch, "E14.23.11", {"start": v(5.95, 26.69) * mm, "mid": v(5.82, 26.85) * mm, "end": v(5.63, 26.95) * mm});
            skArc(sketch, "E15.trimOffspring", {"start": v(-9.37, 21.31) * mm, "mid": v(-10.3, 20.88) * mm, "end": v(-11.2, 20.4) * mm});
            skArc(sketch, "E16.trimOffspring", {"start": v(-14.56, 18.16) * mm, "mid": v(-15.35, 17.5) * mm, "end": v(-16.1, 16.8) * mm});
            skArc(sketch, "E17.trimOffspring", {"start": v(2.54, 23.14) * mm, "mid": v(1.52, 23.23) * mm, "end": v(0.5, 23.27) * mm});
            skArc(sketch, "E18.trimOffspring", {"start": v(-18.77, 13.77) * mm, "mid": v(-19.36, 12.93) * mm, "end": v(-19.9, 12.07) * mm});
            skArc(sketch, "E19.trimOffspring", {"start": v(-21.7, 8.45) * mm, "mid": v(-22.04, 7.48) * mm, "end": v(-22.35, 6.5) * mm});
            skArc(sketch, "E20.trimOffspring", {"start": v(-23.14, 2.54) * mm, "mid": v(-23.23, 1.52) * mm, "end": v(-23.27, 0.5) * mm});
            skArc(sketch, "E21.trimOffspring", {"start": v(-23, -3.53) * mm, "mid": v(-22.83, -4.54) * mm, "end": v(-22.6, -5.54) * mm});
            skArc(sketch, "E22.trimOffspring", {"start": v(-21.31, -9.37) * mm, "mid": v(-20.88, -10.3) * mm, "end": v(-20.4, -11.2) * mm});
            skArc(sketch, "E23.trimOffspring", {"start": v(-18.16, -14.56) * mm, "mid": v(-17.5, -15.35) * mm, "end": v(-16.8, -16.1) * mm});
            skArc(sketch, "E24.trimOffspring", {"start": v(-13.77, -18.77) * mm, "mid": v(-12.93, -19.36) * mm, "end": v(-12.07, -19.9) * mm});
            skArc(sketch, "E25.trimOffspring", {"start": v(-8.45, -21.7) * mm, "mid": v(-7.48, -22.04) * mm, "end": v(-6.5, -22.35) * mm});
            skArc(sketch, "E26.trimOffspring", {"start": v(-2.54, -23.14) * mm, "mid": v(-1.52, -23.23) * mm, "end": v(-0.5, -23.27) * mm});
            skArc(sketch, "E27.trimOffspring", {"start": v(3.53, -23) * mm, "mid": v(4.54, -22.83) * mm, "end": v(5.54, -22.6) * mm});
            skArc(sketch, "E28.trimOffspring", {"start": v(9.37, -21.31) * mm, "mid": v(10.3, -20.88) * mm, "end": v(11.2, -20.4) * mm});
            skArc(sketch, "E29.trimOffspring", {"start": v(8.45, 21.7) * mm, "mid": v(7.48, 22.04) * mm, "end": v(6.5, 22.35) * mm});
            skArc(sketch, "E30.trimOffspring", {"start": v(13.77, 18.77) * mm, "mid": v(12.93, 19.36) * mm, "end": v(12.07, 19.9) * mm});
            skArc(sketch, "E31.trimOffspring", {"start": v(18.16, 14.56) * mm, "mid": v(17.5, 15.35) * mm, "end": v(16.8, 16.1) * mm});
            skArc(sketch, "E32.trimOffspring", {"start": v(21.31, 9.37) * mm, "mid": v(20.88, 10.3) * mm, "end": v(20.4, 11.2) * mm});
            skArc(sketch, "E33.trimOffspring", {"start": v(23, 3.53) * mm, "mid": v(22.83, 4.54) * mm, "end": v(22.6, 5.54) * mm});
            skArc(sketch, "E34.trimOffspring", {"start": v(23.14, -2.54) * mm, "mid": v(23.23, -1.52) * mm, "end": v(23.27, -0.5) * mm});
            skArc(sketch, "E35.trimOffspring", {"start": v(21.7, -8.45) * mm, "mid": v(22.04, -7.48) * mm, "end": v(22.35, -6.5) * mm});
            skArc(sketch, "E36.trimOffspring", {"start": v(18.77, -13.77) * mm, "mid": v(19.36, -12.93) * mm, "end": v(19.9, -12.07) * mm});
            skArc(sketch, "E37.trimOffspring", {"start": v(14.56, -18.16) * mm, "mid": v(15.35, -17.5) * mm, "end": v(16.1, -16.8) * mm});
            skSolve(sketch);
        }
        {
            var Q0;
            Q0 = qSketchRegion(id + "F0", true);
            var Q1;
            Q1=makeQuery(id+"F0.imprint","IMPRINT",FACE,{"disambiguationData":[TD([[makeQuery(id+"F0.imprint","IMPRINT",EDGE,{"derivedFrom":sQuery(id+"F0.wireOp",EDGE,"E0")}),1.0]])]});
            extrude(context, id + "F1", {"entities" : qUnion([Q0, Q1]), "depth" : 12.7 * mm});
        }
        {
            var Q0;
            Q0=makeQuery(id+"F1.opExtrude","CAP_FACE",FACE,{"disambiguationData":[OSD([sQuery(id+"F0.wireOp",EDGE,"E0"),sQuery(id+"F0.wireOp",EDGE,"E1.trimOffspring"),sQuery(id+"F0.wireOp",EDGE,"E3"),sQuery(id+"F0.wireOp",EDGE,"E4"),sQuery(id+"F0.wireOp",EDGE,"E5.MirrorCS"),sQuery(id+"F0.wireOp",EDGE,"E6.MirrorCS"),sQuery(id+"F0.wireOp",EDGE,"E7.MirrorCS"),sQuery(id+"F0.wireOp",EDGE,"E8.filletArc"),sQuery(id+"F0.wireOp",EDGE,"E9.filletArc"),sQuery(id+"F0.wireOp",EDGE,"E10.filletArc"),sQuery(id+"F0.wireOp",EDGE,"E11.filletArc"),sQuery(id+"F0.wireOp",EDGE,"E12.filletArc"),sQuery(id+"F0.wireOp",EDGE,"E13.filletArc"),sQuery(id+"F0.wireOp",EDGE,"E14.1.0"),sQuery(id+"F0.wireOp",EDGE,"E14.1.1"),sQuery(id+"F0.wireOp",EDGE,"E14.1.2"),sQuery(id+"F0.wireOp",EDGE,"E14.1.3"),sQuery(id+"F0.wireOp",EDGE,"E14.1.4"),sQuery(id+"F0.wireOp",EDGE,"E14.1.5"),sQuery(id+"F0.wireOp",EDGE,"E14.1.6"),sQuery(id+"F0.wireOp",EDGE,"E14.1.7"),sQuery(id+"F0.wireOp",EDGE,"E14.1.8"),sQuery(id+"F0.wireOp",EDGE,"E14.1.9"),sQuery(id+"F0.wireOp",EDGE,"E14.1.10"),sQuery(id+"F0.wireOp",EDGE,"E14.1.11"),sQuery(id+"F0.wireOp",EDGE,"E14.2.0"),sQuery(id+"F0.wireOp",EDGE,"E14.2.1"),sQuery(id+"F0.wireOp",EDGE,"E14.2.2"),sQuery(id+"F0.wireOp",EDGE,"E14.2.3"),sQuery(id+"F0.wireOp",EDGE,"E14.2.4"),sQuery(id+"F0.wireOp",EDGE,"E14.2.5"),sQuery(id+"F0.wireOp",EDGE,"E14.2.6"),sQuery(id+"F0.wireOp",EDGE,"E14.2.7"),sQuery(id+"F0.wireOp",EDGE,"E14.2.8"),sQuery(id+"F0.wireOp",EDGE,"E14.2.9"),sQuery(id+"F0.wireOp",EDGE,"E14.2.10"),sQuery(id+"F0.wireOp",EDGE,"E14.2.11"),sQuery(id+"F0.wireOp",EDGE,"E14.3.0"),sQuery(id+"F0.wireOp",EDGE,"E14.3.1"),sQuery(id+"F0.wireOp",EDGE,"E14.3.2"),sQuery(id+"F0.wireOp",EDGE,"E14.3.3"),sQuery(id+"F0.wireOp",EDGE,"E14.3.4"),sQuery(id+"F0.wireOp",EDGE,"E14.3.5"),sQuery(id+"F0.wireOp",EDGE,"E14.3.6"),sQuery(id+"F0.wireOp",EDGE,"E14.3.7"),sQuery(id+"F0.wireOp",EDGE,"E14.3.8"),sQuery(id+"F0.wireOp",EDGE,"E14.3.9"),sQuery(id+"F0.wireOp",EDGE,"E14.3.10"),sQuery(id+"F0.wireOp",EDGE,"E14.3.11"),sQuery(id+"F0.wireOp",EDGE,"E14.4.0"),sQuery(id+"F0.wireOp",EDGE,"E14.4.1"),sQuery(id+"F0.wireOp",EDGE,"E14.4.2"),sQuery(id+"F0.wireOp",EDGE,"E14.4.3"),sQuery(id+"F0.wireOp",EDGE,"E14.4.4"),sQuery(id+"F0.wireOp",EDGE,"E14.4.5"),sQuery(id+"F0.wireOp",EDGE,"E14.4.6"),sQuery(id+"F0.wireOp",EDGE,"E14.4.7"),sQuery(id+"F0.wireOp",EDGE,"E14.4.8"),sQuery(id+"F0.wireOp",EDGE,"E14.4.9"),sQuery(id+"F0.wireOp",EDGE,"E14.4.10"),sQuery(id+"F0.wireOp",EDGE,"E14.4.11"),sQuery(id+"F0.wireOp",EDGE,"E14.5.0"),sQuery(id+"F0.wireOp",EDGE,"E14.5.1"),sQuery(id+"F0.wireOp",EDGE,"E14.5.2"),sQuery(id+"F0.wireOp",EDGE,"E14.5.3"),sQuery(id+"F0.wireOp",EDGE,"E14.5.4"),sQuery(id+"F0.wireOp",EDGE,"E14.5.5"),sQuery(id+"F0.wireOp",EDGE,"E14.5.6"),sQuery(id+"F0.wireOp",EDGE,"E14.5.7"),sQuery(id+"F0.wireOp",EDGE,"E14.5.8"),sQuery(id+"F0.wireOp",EDGE,"E14.5.9"),sQuery(id+"F0.wireOp",EDGE,"E14.5.10"),sQuery(id+"F0.wireOp",EDGE,"E14.5.11"),sQuery(id+"F0.wireOp",EDGE,"E14.6.0"),sQuery(id+"F0.wireOp",EDGE,"E14.6.1"),sQuery(id+"F0.wireOp",EDGE,"E14.6.2"),sQuery(id+"F0.wireOp",EDGE,"E14.6.3"),sQuery(id+"F0.wireOp",EDGE,"E14.6.4"),sQuery(id+"F0.wireOp",EDGE,"E14.6.5"),sQuery(id+"F0.wireOp",EDGE,"E14.6.6"),sQuery(id+"F0.wireOp",EDGE,"E14.6.7"),sQuery(id+"F0.wireOp",EDGE,"E14.6.8"),sQuery(id+"F0.wireOp",EDGE,"E14.6.9"),sQuery(id+"F0.wireOp",EDGE,"E14.6.10"),sQuery(id+"F0.wireOp",EDGE,"E14.6.11"),sQuery(id+"F0.wireOp",EDGE,"E14.7.0"),sQuery(id+"F0.wireOp",EDGE,"E14.7.1"),sQuery(id+"F0.wireOp",EDGE,"E14.7.2"),sQuery(id+"F0.wireOp",EDGE,"E14.7.3"),sQuery(id+"F0.wireOp",EDGE,"E14.7.4"),sQuery(id+"F0.wireOp",EDGE,"E14.7.5"),sQuery(id+"F0.wireOp",EDGE,"E14.7.6"),sQuery(id+"F0.wireOp",EDGE,"E14.7.7"),sQuery(id+"F0.wireOp",EDGE,"E14.7.8"),sQuery(id+"F0.wireOp",EDGE,"E14.7.9"),sQuery(id+"F0.wireOp",EDGE,"E14.7.10"),sQuery(id+"F0.wireOp",EDGE,"E14.7.11"),sQuery(id+"F0.wireOp",EDGE,"E14.8.0"),sQuery(id+"F0.wireOp",EDGE,"E14.8.1"),sQuery(id+"F0.wireOp",EDGE,"E14.8.2"),sQuery(id+"F0.wireOp",EDGE,"E14.8.3"),sQuery(id+"F0.wireOp",EDGE,"E14.8.4"),sQuery(id+"F0.wireOp",EDGE,"E14.8.5"),sQuery(id+"F0.wireOp",EDGE,"E14.8.6"),sQuery(id+"F0.wireOp",EDGE,"E14.8.7"),sQuery(id+"F0.wireOp",EDGE,"E14.8.8"),sQuery(id+"F0.wireOp",EDGE,"E14.8.9"),sQuery(id+"F0.wireOp",EDGE,"E14.8.10"),sQuery(id+"F0.wireOp",EDGE,"E14.8.11"),sQuery(id+"F0.wireOp",EDGE,"E14.9.0"),sQuery(id+"F0.wireOp",EDGE,"E14.9.1"),sQuery(id+"F0.wireOp",EDGE,"E14.9.2"),sQuery(id+"F0.wireOp",EDGE,"E14.9.3"),sQuery(id+"F0.wireOp",EDGE,"E14.9.4"),sQuery(id+"F0.wireOp",EDGE,"E14.9.5"),sQuery(id+"F0.wireOp",EDGE,"E14.9.6"),sQuery(id+"F0.wireOp",EDGE,"E14.9.7"),sQuery(id+"F0.wireOp",EDGE,"E14.9.8"),sQuery(id+"F0.wireOp",EDGE,"E14.9.9"),sQuery(id+"F0.wireOp",EDGE,"E14.9.10"),sQuery(id+"F0.wireOp",EDGE,"E14.9.11"),sQuery(id+"F0.wireOp",EDGE,"E14.10.0"),sQuery(id+"F0.wireOp",EDGE,"E14.10.1"),sQuery(id+"F0.wireOp",EDGE,"E14.10.2"),sQuery(id+"F0.wireOp",EDGE,"E14.10.3"),sQuery(id+"F0.wireOp",EDGE,"E14.10.4"),sQuery(id+"F0.wireOp",EDGE,"E14.10.5"),sQuery(id+"F0.wireOp",EDGE,"E14.10.6"),sQuery(id+"F0.wireOp",EDGE,"E14.10.7"),sQuery(id+"F0.wireOp",EDGE,"E14.10.8"),sQuery(id+"F0.wireOp",EDGE,"E14.10.9"),sQuery(id+"F0.wireOp",EDGE,"E14.10.10"),sQuery(id+"F0.wireOp",EDGE,"E14.10.11"),sQuery(id+"F0.wireOp",EDGE,"E14.11.0"),sQuery(id+"F0.wireOp",EDGE,"E14.11.1"),sQuery(id+"F0.wireOp",EDGE,"E14.11.2"),sQuery(id+"F0.wireOp",EDGE,"E14.11.3"),sQuery(id+"F0.wireOp",EDGE,"E14.11.4"),sQuery(id+"F0.wireOp",EDGE,"E14.11.5"),sQuery(id+"F0.wireOp",EDGE,"E14.11.6"),sQuery(id+"F0.wireOp",EDGE,"E14.11.7"),sQuery(id+"F0.wireOp",EDGE,"E14.11.8"),sQuery(id+"F0.wireOp",EDGE,"E14.11.9"),sQuery(id+"F0.wireOp",EDGE,"E14.11.10"),sQuery(id+"F0.wireOp",EDGE,"E14.11.11"),sQuery(id+"F0.wireOp",EDGE,"E14.12.0"),sQuery(id+"F0.wireOp",EDGE,"E14.12.1"),sQuery(id+"F0.wireOp",EDGE,"E14.12.2"),sQuery(id+"F0.wireOp",EDGE,"E14.12.3"),sQuery(id+"F0.wireOp",EDGE,"E14.12.4"),sQuery(id+"F0.wireOp",EDGE,"E14.12.5"),sQuery(id+"F0.wireOp",EDGE,"E14.12.6"),sQuery(id+"F0.wireOp",EDGE,"E14.12.7"),sQuery(id+"F0.wireOp",EDGE,"E14.12.8"),sQuery(id+"F0.wireOp",EDGE,"E14.12.9"),sQuery(id+"F0.wireOp",EDGE,"E14.12.10"),sQuery(id+"F0.wireOp",EDGE,"E14.12.11"),sQuery(id+"F0.wireOp",EDGE,"E14.13.0"),sQuery(id+"F0.wireOp",EDGE,"E14.13.1"),sQuery(id+"F0.wireOp",EDGE,"E14.13.2"),sQuery(id+"F0.wireOp",EDGE,"E14.13.3"),sQuery(id+"F0.wireOp",EDGE,"E14.13.4"),sQuery(id+"F0.wireOp",EDGE,"E14.13.5"),sQuery(id+"F0.wireOp",EDGE,"E14.13.6"),sQuery(id+"F0.wireOp",EDGE,"E14.13.7"),sQuery(id+"F0.wireOp",EDGE,"E14.13.8"),sQuery(id+"F0.wireOp",EDGE,"E14.13.9"),sQuery(id+"F0.wireOp",EDGE,"E14.13.10"),sQuery(id+"F0.wireOp",EDGE,"E14.13.11"),sQuery(id+"F0.wireOp",EDGE,"E14.14.0"),sQuery(id+"F0.wireOp",EDGE,"E14.14.1"),sQuery(id+"F0.wireOp",EDGE,"E14.14.2"),sQuery(id+"F0.wireOp",EDGE,"E14.14.3"),sQuery(id+"F0.wireOp",EDGE,"E14.14.4"),sQuery(id+"F0.wireOp",EDGE,"E14.14.5"),sQuery(id+"F0.wireOp",EDGE,"E14.14.6"),sQuery(id+"F0.wireOp",EDGE,"E14.14.7"),sQuery(id+"F0.wireOp",EDGE,"E14.14.8"),sQuery(id+"F0.wireOp",EDGE,"E14.14.9"),sQuery(id+"F0.wireOp",EDGE,"E14.14.10"),sQuery(id+"F0.wireOp",EDGE,"E14.14.11"),sQuery(id+"F0.wireOp",EDGE,"E14.15.0"),sQuery(id+"F0.wireOp",EDGE,"E14.15.1"),sQuery(id+"F0.wireOp",EDGE,"E14.15.2"),sQuery(id+"F0.wireOp",EDGE,"E14.15.3"),sQuery(id+"F0.wireOp",EDGE,"E14.15.4"),sQuery(id+"F0.wireOp",EDGE,"E14.15.5"),sQuery(id+"F0.wireOp",EDGE,"E14.15.6"),sQuery(id+"F0.wireOp",EDGE,"E14.15.7"),sQuery(id+"F0.wireOp",EDGE,"E14.15.8"),sQuery(id+"F0.wireOp",EDGE,"E14.15.9"),sQuery(id+"F0.wireOp",EDGE,"E14.15.10"),sQuery(id+"F0.wireOp",EDGE,"E14.15.11"),sQuery(id+"F0.wireOp",EDGE,"E14.16.0"),sQuery(id+"F0.wireOp",EDGE,"E14.16.1"),sQuery(id+"F0.wireOp",EDGE,"E14.16.2"),sQuery(id+"F0.wireOp",EDGE,"E14.16.3"),sQuery(id+"F0.wireOp",EDGE,"E14.16.4"),sQuery(id+"F0.wireOp",EDGE,"E14.16.5"),sQuery(id+"F0.wireOp",EDGE,"E14.16.6"),sQuery(id+"F0.wireOp",EDGE,"E14.16.7"),sQuery(id+"F0.wireOp",EDGE,"E14.16.8"),sQuery(id+"F0.wireOp",EDGE,"E14.16.9"),sQuery(id+"F0.wireOp",EDGE,"E14.16.10"),sQuery(id+"F0.wireOp",EDGE,"E14.16.11"),sQuery(id+"F0.wireOp",EDGE,"E14.17.0"),sQuery(id+"F0.wireOp",EDGE,"E14.17.1"),sQuery(id+"F0.wireOp",EDGE,"E14.17.2"),sQuery(id+"F0.wireOp",EDGE,"E14.17.3"),sQuery(id+"F0.wireOp",EDGE,"E14.17.4"),sQuery(id+"F0.wireOp",EDGE,"E14.17.5"),sQuery(id+"F0.wireOp",EDGE,"E14.17.6"),sQuery(id+"F0.wireOp",EDGE,"E14.17.7"),sQuery(id+"F0.wireOp",EDGE,"E14.17.8"),sQuery(id+"F0.wireOp",EDGE,"E14.17.9"),sQuery(id+"F0.wireOp",EDGE,"E14.17.10"),sQuery(id+"F0.wireOp",EDGE,"E14.17.11"),sQuery(id+"F0.wireOp",EDGE,"E14.18.0"),sQuery(id+"F0.wireOp",EDGE,"E14.18.1"),sQuery(id+"F0.wireOp",EDGE,"E14.18.2"),sQuery(id+"F0.wireOp",EDGE,"E14.18.3"),sQuery(id+"F0.wireOp",EDGE,"E14.18.4"),sQuery(id+"F0.wireOp",EDGE,"E14.18.5"),sQuery(id+"F0.wireOp",EDGE,"E14.18.6"),sQuery(id+"F0.wireOp",EDGE,"E14.18.7"),sQuery(id+"F0.wireOp",EDGE,"E14.18.8"),sQuery(id+"F0.wireOp",EDGE,"E14.18.9"),sQuery(id+"F0.wireOp",EDGE,"E14.18.10"),sQuery(id+"F0.wireOp",EDGE,"E14.18.11"),sQuery(id+"F0.wireOp",EDGE,"E14.19.0"),sQuery(id+"F0.wireOp",EDGE,"E14.19.1"),sQuery(id+"F0.wireOp",EDGE,"E14.19.2"),sQuery(id+"F0.wireOp",EDGE,"E14.19.3"),sQuery(id+"F0.wireOp",EDGE,"E14.19.4"),sQuery(id+"F0.wireOp",EDGE,"E14.19.5"),sQuery(id+"F0.wireOp",EDGE,"E14.19.6"),sQuery(id+"F0.wireOp",EDGE,"E14.19.7"),sQuery(id+"F0.wireOp",EDGE,"E14.19.8"),sQuery(id+"F0.wireOp",EDGE,"E14.19.9"),sQuery(id+"F0.wireOp",EDGE,"E14.19.10"),sQuery(id+"F0.wireOp",EDGE,"E14.19.11"),sQuery(id+"F0.wireOp",EDGE,"E14.20.0"),sQuery(id+"F0.wireOp",EDGE,"E14.20.1"),sQuery(id+"F0.wireOp",EDGE,"E14.20.2"),sQuery(id+"F0.wireOp",EDGE,"E14.20.3"),sQuery(id+"F0.wireOp",EDGE,"E14.20.4"),sQuery(id+"F0.wireOp",EDGE,"E14.20.5"),sQuery(id+"F0.wireOp",EDGE,"E14.20.6"),sQuery(id+"F0.wireOp",EDGE,"E14.20.7"),sQuery(id+"F0.wireOp",EDGE,"E14.20.8"),sQuery(id+"F0.wireOp",EDGE,"E14.20.9"),sQuery(id+"F0.wireOp",EDGE,"E14.20.10"),sQuery(id+"F0.wireOp",EDGE,"E14.20.11"),sQuery(id+"F0.wireOp",EDGE,"E14.21.0"),sQuery(id+"F0.wireOp",EDGE,"E14.21.1"),sQuery(id+"F0.wireOp",EDGE,"E14.21.2"),sQuery(id+"F0.wireOp",EDGE,"E14.21.3"),sQuery(id+"F0.wireOp",EDGE,"E14.21.4"),sQuery(id+"F0.wireOp",EDGE,"E14.21.5"),sQuery(id+"F0.wireOp",EDGE,"E14.21.6"),sQuery(id+"F0.wireOp",EDGE,"E14.21.7"),sQuery(id+"F0.wireOp",EDGE,"E14.21.8"),sQuery(id+"F0.wireOp",EDGE,"E14.21.9"),sQuery(id+"F0.wireOp",EDGE,"E14.21.10"),sQuery(id+"F0.wireOp",EDGE,"E14.21.11"),sQuery(id+"F0.wireOp",EDGE,"E14.22.0"),sQuery(id+"F0.wireOp",EDGE,"E14.22.1"),sQuery(id+"F0.wireOp",EDGE,"E14.22.2"),sQuery(id+"F0.wireOp",EDGE,"E14.22.3"),sQuery(id+"F0.wireOp",EDGE,"E14.22.4"),sQuery(id+"F0.wireOp",EDGE,"E14.22.5"),sQuery(id+"F0.wireOp",EDGE,"E14.22.6"),sQuery(id+"F0.wireOp",EDGE,"E14.22.7"),sQuery(id+"F0.wireOp",EDGE,"E14.22.8"),sQuery(id+"F0.wireOp",EDGE,"E14.22.9"),sQuery(id+"F0.wireOp",EDGE,"E14.22.10"),sQuery(id+"F0.wireOp",EDGE,"E14.22.11"),sQuery(id+"F0.wireOp",EDGE,"E14.23.0"),sQuery(id+"F0.wireOp",EDGE,"E14.23.1"),sQuery(id+"F0.wireOp",EDGE,"E14.23.2"),sQuery(id+"F0.wireOp",EDGE,"E14.23.3"),sQuery(id+"F0.wireOp",EDGE,"E14.23.4"),sQuery(id+"F0.wireOp",EDGE,"E14.23.5"),sQuery(id+"F0.wireOp",EDGE,"E14.23.6"),sQuery(id+"F0.wireOp",EDGE,"E14.23.7"),sQuery(id+"F0.wireOp",EDGE,"E14.23.8"),sQuery(id+"F0.wireOp",EDGE,"E14.23.9"),sQuery(id+"F0.wireOp",EDGE,"E14.23.10"),sQuery(id+"F0.wireOp",EDGE,"E14.23.11"),sQuery(id+"F0.wireOp",EDGE,"E15.trimOffspring"),sQuery(id+"F0.wireOp",EDGE,"E16.trimOffspring"),sQuery(id+"F0.wireOp",EDGE,"E17.trimOffspring"),sQuery(id+"F0.wireOp",EDGE,"E18.trimOffspring"),sQuery(id+"F0.wireOp",EDGE,"E19.trimOffspring"),sQuery(id+"F0.wireOp",EDGE,"E20.trimOffspring"),sQuery(id+"F0.wireOp",EDGE,"E21.trimOffspring"),sQuery(id+"F0.wireOp",EDGE,"E22.trimOffspring"),sQuery(id+"F0.wireOp",EDGE,"E23.trimOffspring"),sQuery(id+"F0.wireOp",EDGE,"E24.trimOffspring"),sQuery(id+"F0.wireOp",EDGE,"E25.trimOffspring"),sQuery(id+"F0.wireOp",EDGE,"E26.trimOffspring"),sQuery(id+"F0.wireOp",EDGE,"E27.trimOffspring"),sQuery(id+"F0.wireOp",EDGE,"E28.trimOffspring"),sQuery(id+"F0.wireOp",EDGE,"E29.trimOffspring"),sQuery(id+"F0.wireOp",EDGE,"E30.trimOffspring"),sQuery(id+"F0.wireOp",EDGE,"E31.trimOffspring"),sQuery(id+"F0.wireOp",EDGE,"E32.trimOffspring"),sQuery(id+"F0.wireOp",EDGE,"E33.trimOffspring"),sQuery(id+"F0.wireOp",EDGE,"E34.trimOffspring"),sQuery(id+"F0.wireOp",EDGE,"E35.trimOffspring"),sQuery(id+"F0.wireOp",EDGE,"E36.trimOffspring"),sQuery(id+"F0.wireOp",EDGE,"E37.trimOffspring")])],"isStart":false});
            var sketch = newSketch(context, id + "F2", { "sketchPlane" : qUnion([Q0])});
            skCircle(sketch, "E38", {"center": v(0, 0) * mm, "radius": 6.35 * mm});
            skSolve(sketch);
        }
        {
            var Q0;
            Q0 = qSketchRegion(id + "F2", true);
            extrude(context, id + "F3", {"entities" : qUnion([Q0]), "operationType" : NewBodyOperationType.ADD, "depth" : 25.4 * mm});
        }
        {
            var Q0;
            Q0=makeQuery(id+"F1.opExtrude","CAP_FACE",FACE,{"disambiguationData":[OSD([sQuery(id+"F0.wireOp",EDGE,"E0"),sQuery(id+"F0.wireOp",EDGE,"E1.trimOffspring"),sQuery(id+"F0.wireOp",EDGE,"E3"),sQuery(id+"F0.wireOp",EDGE,"E4"),sQuery(id+"F0.wireOp",EDGE,"E5.MirrorCS"),sQuery(id+"F0.wireOp",EDGE,"E6.MirrorCS"),sQuery(id+"F0.wireOp",EDGE,"E7.MirrorCS"),sQuery(id+"F0.wireOp",EDGE,"E8.filletArc"),sQuery(id+"F0.wireOp",EDGE,"E9.filletArc"),sQuery(id+"F0.wireOp",EDGE,"E10.filletArc"),sQuery(id+"F0.wireOp",EDGE,"E11.filletArc"),sQuery(id+"F0.wireOp",EDGE,"E12.filletArc"),sQuery(id+"F0.wireOp",EDGE,"E13.filletArc"),sQuery(id+"F0.wireOp",EDGE,"E14.1.0"),sQuery(id+"F0.wireOp",EDGE,"E14.1.1"),sQuery(id+"F0.wireOp",EDGE,"E14.1.2"),sQuery(id+"F0.wireOp",EDGE,"E14.1.3"),sQuery(id+"F0.wireOp",EDGE,"E14.1.4"),sQuery(id+"F0.wireOp",EDGE,"E14.1.5"),sQuery(id+"F0.wireOp",EDGE,"E14.1.6"),sQuery(id+"F0.wireOp",EDGE,"E14.1.7"),sQuery(id+"F0.wireOp",EDGE,"E14.1.8"),sQuery(id+"F0.wireOp",EDGE,"E14.1.9"),sQuery(id+"F0.wireOp",EDGE,"E14.1.10"),sQuery(id+"F0.wireOp",EDGE,"E14.1.11"),sQuery(id+"F0.wireOp",EDGE,"E14.2.0"),sQuery(id+"F0.wireOp",EDGE,"E14.2.1"),sQuery(id+"F0.wireOp",EDGE,"E14.2.2"),sQuery(id+"F0.wireOp",EDGE,"E14.2.3"),sQuery(id+"F0.wireOp",EDGE,"E14.2.4"),sQuery(id+"F0.wireOp",EDGE,"E14.2.5"),sQuery(id+"F0.wireOp",EDGE,"E14.2.6"),sQuery(id+"F0.wireOp",EDGE,"E14.2.7"),sQuery(id+"F0.wireOp",EDGE,"E14.2.8"),sQuery(id+"F0.wireOp",EDGE,"E14.2.9"),sQuery(id+"F0.wireOp",EDGE,"E14.2.10"),sQuery(id+"F0.wireOp",EDGE,"E14.2.11"),sQuery(id+"F0.wireOp",EDGE,"E14.3.0"),sQuery(id+"F0.wireOp",EDGE,"E14.3.1"),sQuery(id+"F0.wireOp",EDGE,"E14.3.2"),sQuery(id+"F0.wireOp",EDGE,"E14.3.3"),sQuery(id+"F0.wireOp",EDGE,"E14.3.4"),sQuery(id+"F0.wireOp",EDGE,"E14.3.5"),sQuery(id+"F0.wireOp",EDGE,"E14.3.6"),sQuery(id+"F0.wireOp",EDGE,"E14.3.7"),sQuery(id+"F0.wireOp",EDGE,"E14.3.8"),sQuery(id+"F0.wireOp",EDGE,"E14.3.9"),sQuery(id+"F0.wireOp",EDGE,"E14.3.10"),sQuery(id+"F0.wireOp",EDGE,"E14.3.11"),sQuery(id+"F0.wireOp",EDGE,"E14.4.0"),sQuery(id+"F0.wireOp",EDGE,"E14.4.1"),sQuery(id+"F0.wireOp",EDGE,"E14.4.2"),sQuery(id+"F0.wireOp",EDGE,"E14.4.3"),sQuery(id+"F0.wireOp",EDGE,"E14.4.4"),sQuery(id+"F0.wireOp",EDGE,"E14.4.5"),sQuery(id+"F0.wireOp",EDGE,"E14.4.6"),sQuery(id+"F0.wireOp",EDGE,"E14.4.7"),sQuery(id+"F0.wireOp",EDGE,"E14.4.8"),sQuery(id+"F0.wireOp",EDGE,"E14.4.9"),sQuery(id+"F0.wireOp",EDGE,"E14.4.10"),sQuery(id+"F0.wireOp",EDGE,"E14.4.11"),sQuery(id+"F0.wireOp",EDGE,"E14.5.0"),sQuery(id+"F0.wireOp",EDGE,"E14.5.1"),sQuery(id+"F0.wireOp",EDGE,"E14.5.2"),sQuery(id+"F0.wireOp",EDGE,"E14.5.3"),sQuery(id+"F0.wireOp",EDGE,"E14.5.4"),sQuery(id+"F0.wireOp",EDGE,"E14.5.5"),sQuery(id+"F0.wireOp",EDGE,"E14.5.6"),sQuery(id+"F0.wireOp",EDGE,"E14.5.7"),sQuery(id+"F0.wireOp",EDGE,"E14.5.8"),sQuery(id+"F0.wireOp",EDGE,"E14.5.9"),sQuery(id+"F0.wireOp",EDGE,"E14.5.10"),sQuery(id+"F0.wireOp",EDGE,"E14.5.11"),sQuery(id+"F0.wireOp",EDGE,"E14.6.0"),sQuery(id+"F0.wireOp",EDGE,"E14.6.1"),sQuery(id+"F0.wireOp",EDGE,"E14.6.2"),sQuery(id+"F0.wireOp",EDGE,"E14.6.3"),sQuery(id+"F0.wireOp",EDGE,"E14.6.4"),sQuery(id+"F0.wireOp",EDGE,"E14.6.5"),sQuery(id+"F0.wireOp",EDGE,"E14.6.6"),sQuery(id+"F0.wireOp",EDGE,"E14.6.7"),sQuery(id+"F0.wireOp",EDGE,"E14.6.8"),sQuery(id+"F0.wireOp",EDGE,"E14.6.9"),sQuery(id+"F0.wireOp",EDGE,"E14.6.10"),sQuery(id+"F0.wireOp",EDGE,"E14.6.11"),sQuery(id+"F0.wireOp",EDGE,"E14.7.0"),sQuery(id+"F0.wireOp",EDGE,"E14.7.1"),sQuery(id+"F0.wireOp",EDGE,"E14.7.2"),sQuery(id+"F0.wireOp",EDGE,"E14.7.3"),sQuery(id+"F0.wireOp",EDGE,"E14.7.4"),sQuery(id+"F0.wireOp",EDGE,"E14.7.5"),sQuery(id+"F0.wireOp",EDGE,"E14.7.6"),sQuery(id+"F0.wireOp",EDGE,"E14.7.7"),sQuery(id+"F0.wireOp",EDGE,"E14.7.8"),sQuery(id+"F0.wireOp",EDGE,"E14.7.9"),sQuery(id+"F0.wireOp",EDGE,"E14.7.10"),sQuery(id+"F0.wireOp",EDGE,"E14.7.11"),sQuery(id+"F0.wireOp",EDGE,"E14.8.0"),sQuery(id+"F0.wireOp",EDGE,"E14.8.1"),sQuery(id+"F0.wireOp",EDGE,"E14.8.2"),sQuery(id+"F0.wireOp",EDGE,"E14.8.3"),sQuery(id+"F0.wireOp",EDGE,"E14.8.4"),sQuery(id+"F0.wireOp",EDGE,"E14.8.5"),sQuery(id+"F0.wireOp",EDGE,"E14.8.6"),sQuery(id+"F0.wireOp",EDGE,"E14.8.7"),sQuery(id+"F0.wireOp",EDGE,"E14.8.8"),sQuery(id+"F0.wireOp",EDGE,"E14.8.9"),sQuery(id+"F0.wireOp",EDGE,"E14.8.10"),sQuery(id+"F0.wireOp",EDGE,"E14.8.11"),sQuery(id+"F0.wireOp",EDGE,"E14.9.0"),sQuery(id+"F0.wireOp",EDGE,"E14.9.1"),sQuery(id+"F0.wireOp",EDGE,"E14.9.2"),sQuery(id+"F0.wireOp",EDGE,"E14.9.3"),sQuery(id+"F0.wireOp",EDGE,"E14.9.4"),sQuery(id+"F0.wireOp",EDGE,"E14.9.5"),sQuery(id+"F0.wireOp",EDGE,"E14.9.6"),sQuery(id+"F0.wireOp",EDGE,"E14.9.7"),sQuery(id+"F0.wireOp",EDGE,"E14.9.8"),sQuery(id+"F0.wireOp",EDGE,"E14.9.9"),sQuery(id+"F0.wireOp",EDGE,"E14.9.10"),sQuery(id+"F0.wireOp",EDGE,"E14.9.11"),sQuery(id+"F0.wireOp",EDGE,"E14.10.0"),sQuery(id+"F0.wireOp",EDGE,"E14.10.1"),sQuery(id+"F0.wireOp",EDGE,"E14.10.2"),sQuery(id+"F0.wireOp",EDGE,"E14.10.3"),sQuery(id+"F0.wireOp",EDGE,"E14.10.4"),sQuery(id+"F0.wireOp",EDGE,"E14.10.5"),sQuery(id+"F0.wireOp",EDGE,"E14.10.6"),sQuery(id+"F0.wireOp",EDGE,"E14.10.7"),sQuery(id+"F0.wireOp",EDGE,"E14.10.8"),sQuery(id+"F0.wireOp",EDGE,"E14.10.9"),sQuery(id+"F0.wireOp",EDGE,"E14.10.10"),sQuery(id+"F0.wireOp",EDGE,"E14.10.11"),sQuery(id+"F0.wireOp",EDGE,"E14.11.0"),sQuery(id+"F0.wireOp",EDGE,"E14.11.1"),sQuery(id+"F0.wireOp",EDGE,"E14.11.2"),sQuery(id+"F0.wireOp",EDGE,"E14.11.3"),sQuery(id+"F0.wireOp",EDGE,"E14.11.4"),sQuery(id+"F0.wireOp",EDGE,"E14.11.5"),sQuery(id+"F0.wireOp",EDGE,"E14.11.6"),sQuery(id+"F0.wireOp",EDGE,"E14.11.7"),sQuery(id+"F0.wireOp",EDGE,"E14.11.8"),sQuery(id+"F0.wireOp",EDGE,"E14.11.9"),sQuery(id+"F0.wireOp",EDGE,"E14.11.10"),sQuery(id+"F0.wireOp",EDGE,"E14.11.11"),sQuery(id+"F0.wireOp",EDGE,"E14.12.0"),sQuery(id+"F0.wireOp",EDGE,"E14.12.1"),sQuery(id+"F0.wireOp",EDGE,"E14.12.2"),sQuery(id+"F0.wireOp",EDGE,"E14.12.3"),sQuery(id+"F0.wireOp",EDGE,"E14.12.4"),sQuery(id+"F0.wireOp",EDGE,"E14.12.5"),sQuery(id+"F0.wireOp",EDGE,"E14.12.6"),sQuery(id+"F0.wireOp",EDGE,"E14.12.7"),sQuery(id+"F0.wireOp",EDGE,"E14.12.8"),sQuery(id+"F0.wireOp",EDGE,"E14.12.9"),sQuery(id+"F0.wireOp",EDGE,"E14.12.10"),sQuery(id+"F0.wireOp",EDGE,"E14.12.11"),sQuery(id+"F0.wireOp",EDGE,"E14.13.0"),sQuery(id+"F0.wireOp",EDGE,"E14.13.1"),sQuery(id+"F0.wireOp",EDGE,"E14.13.2"),sQuery(id+"F0.wireOp",EDGE,"E14.13.3"),sQuery(id+"F0.wireOp",EDGE,"E14.13.4"),sQuery(id+"F0.wireOp",EDGE,"E14.13.5"),sQuery(id+"F0.wireOp",EDGE,"E14.13.6"),sQuery(id+"F0.wireOp",EDGE,"E14.13.7"),sQuery(id+"F0.wireOp",EDGE,"E14.13.8"),sQuery(id+"F0.wireOp",EDGE,"E14.13.9"),sQuery(id+"F0.wireOp",EDGE,"E14.13.10"),sQuery(id+"F0.wireOp",EDGE,"E14.13.11"),sQuery(id+"F0.wireOp",EDGE,"E14.14.0"),sQuery(id+"F0.wireOp",EDGE,"E14.14.1"),sQuery(id+"F0.wireOp",EDGE,"E14.14.2"),sQuery(id+"F0.wireOp",EDGE,"E14.14.3"),sQuery(id+"F0.wireOp",EDGE,"E14.14.4"),sQuery(id+"F0.wireOp",EDGE,"E14.14.5"),sQuery(id+"F0.wireOp",EDGE,"E14.14.6"),sQuery(id+"F0.wireOp",EDGE,"E14.14.7"),sQuery(id+"F0.wireOp",EDGE,"E14.14.8"),sQuery(id+"F0.wireOp",EDGE,"E14.14.9"),sQuery(id+"F0.wireOp",EDGE,"E14.14.10"),sQuery(id+"F0.wireOp",EDGE,"E14.14.11"),sQuery(id+"F0.wireOp",EDGE,"E14.15.0"),sQuery(id+"F0.wireOp",EDGE,"E14.15.1"),sQuery(id+"F0.wireOp",EDGE,"E14.15.2"),sQuery(id+"F0.wireOp",EDGE,"E14.15.3"),sQuery(id+"F0.wireOp",EDGE,"E14.15.4"),sQuery(id+"F0.wireOp",EDGE,"E14.15.5"),sQuery(id+"F0.wireOp",EDGE,"E14.15.6"),sQuery(id+"F0.wireOp",EDGE,"E14.15.7"),sQuery(id+"F0.wireOp",EDGE,"E14.15.8"),sQuery(id+"F0.wireOp",EDGE,"E14.15.9"),sQuery(id+"F0.wireOp",EDGE,"E14.15.10"),sQuery(id+"F0.wireOp",EDGE,"E14.15.11"),sQuery(id+"F0.wireOp",EDGE,"E14.16.0"),sQuery(id+"F0.wireOp",EDGE,"E14.16.1"),sQuery(id+"F0.wireOp",EDGE,"E14.16.2"),sQuery(id+"F0.wireOp",EDGE,"E14.16.3"),sQuery(id+"F0.wireOp",EDGE,"E14.16.4"),sQuery(id+"F0.wireOp",EDGE,"E14.16.5"),sQuery(id+"F0.wireOp",EDGE,"E14.16.6"),sQuery(id+"F0.wireOp",EDGE,"E14.16.7"),sQuery(id+"F0.wireOp",EDGE,"E14.16.8"),sQuery(id+"F0.wireOp",EDGE,"E14.16.9"),sQuery(id+"F0.wireOp",EDGE,"E14.16.10"),sQuery(id+"F0.wireOp",EDGE,"E14.16.11"),sQuery(id+"F0.wireOp",EDGE,"E14.17.0"),sQuery(id+"F0.wireOp",EDGE,"E14.17.1"),sQuery(id+"F0.wireOp",EDGE,"E14.17.2"),sQuery(id+"F0.wireOp",EDGE,"E14.17.3"),sQuery(id+"F0.wireOp",EDGE,"E14.17.4"),sQuery(id+"F0.wireOp",EDGE,"E14.17.5"),sQuery(id+"F0.wireOp",EDGE,"E14.17.6"),sQuery(id+"F0.wireOp",EDGE,"E14.17.7"),sQuery(id+"F0.wireOp",EDGE,"E14.17.8"),sQuery(id+"F0.wireOp",EDGE,"E14.17.9"),sQuery(id+"F0.wireOp",EDGE,"E14.17.10"),sQuery(id+"F0.wireOp",EDGE,"E14.17.11"),sQuery(id+"F0.wireOp",EDGE,"E14.18.0"),sQuery(id+"F0.wireOp",EDGE,"E14.18.1"),sQuery(id+"F0.wireOp",EDGE,"E14.18.2"),sQuery(id+"F0.wireOp",EDGE,"E14.18.3"),sQuery(id+"F0.wireOp",EDGE,"E14.18.4"),sQuery(id+"F0.wireOp",EDGE,"E14.18.5"),sQuery(id+"F0.wireOp",EDGE,"E14.18.6"),sQuery(id+"F0.wireOp",EDGE,"E14.18.7"),sQuery(id+"F0.wireOp",EDGE,"E14.18.8"),sQuery(id+"F0.wireOp",EDGE,"E14.18.9"),sQuery(id+"F0.wireOp",EDGE,"E14.18.10"),sQuery(id+"F0.wireOp",EDGE,"E14.18.11"),sQuery(id+"F0.wireOp",EDGE,"E14.19.0"),sQuery(id+"F0.wireOp",EDGE,"E14.19.1"),sQuery(id+"F0.wireOp",EDGE,"E14.19.2"),sQuery(id+"F0.wireOp",EDGE,"E14.19.3"),sQuery(id+"F0.wireOp",EDGE,"E14.19.4"),sQuery(id+"F0.wireOp",EDGE,"E14.19.5"),sQuery(id+"F0.wireOp",EDGE,"E14.19.6"),sQuery(id+"F0.wireOp",EDGE,"E14.19.7"),sQuery(id+"F0.wireOp",EDGE,"E14.19.8"),sQuery(id+"F0.wireOp",EDGE,"E14.19.9"),sQuery(id+"F0.wireOp",EDGE,"E14.19.10"),sQuery(id+"F0.wireOp",EDGE,"E14.19.11"),sQuery(id+"F0.wireOp",EDGE,"E14.20.0"),sQuery(id+"F0.wireOp",EDGE,"E14.20.1"),sQuery(id+"F0.wireOp",EDGE,"E14.20.2"),sQuery(id+"F0.wireOp",EDGE,"E14.20.3"),sQuery(id+"F0.wireOp",EDGE,"E14.20.4"),sQuery(id+"F0.wireOp",EDGE,"E14.20.5"),sQuery(id+"F0.wireOp",EDGE,"E14.20.6"),sQuery(id+"F0.wireOp",EDGE,"E14.20.7"),sQuery(id+"F0.wireOp",EDGE,"E14.20.8"),sQuery(id+"F0.wireOp",EDGE,"E14.20.9"),sQuery(id+"F0.wireOp",EDGE,"E14.20.10"),sQuery(id+"F0.wireOp",EDGE,"E14.20.11"),sQuery(id+"F0.wireOp",EDGE,"E14.21.0"),sQuery(id+"F0.wireOp",EDGE,"E14.21.1"),sQuery(id+"F0.wireOp",EDGE,"E14.21.2"),sQuery(id+"F0.wireOp",EDGE,"E14.21.3"),sQuery(id+"F0.wireOp",EDGE,"E14.21.4"),sQuery(id+"F0.wireOp",EDGE,"E14.21.5"),sQuery(id+"F0.wireOp",EDGE,"E14.21.6"),sQuery(id+"F0.wireOp",EDGE,"E14.21.7"),sQuery(id+"F0.wireOp",EDGE,"E14.21.8"),sQuery(id+"F0.wireOp",EDGE,"E14.21.9"),sQuery(id+"F0.wireOp",EDGE,"E14.21.10"),sQuery(id+"F0.wireOp",EDGE,"E14.21.11"),sQuery(id+"F0.wireOp",EDGE,"E14.22.0"),sQuery(id+"F0.wireOp",EDGE,"E14.22.1"),sQuery(id+"F0.wireOp",EDGE,"E14.22.2"),sQuery(id+"F0.wireOp",EDGE,"E14.22.3"),sQuery(id+"F0.wireOp",EDGE,"E14.22.4"),sQuery(id+"F0.wireOp",EDGE,"E14.22.5"),sQuery(id+"F0.wireOp",EDGE,"E14.22.6"),sQuery(id+"F0.wireOp",EDGE,"E14.22.7"),sQuery(id+"F0.wireOp",EDGE,"E14.22.8"),sQuery(id+"F0.wireOp",EDGE,"E14.22.9"),sQuery(id+"F0.wireOp",EDGE,"E14.22.10"),sQuery(id+"F0.wireOp",EDGE,"E14.22.11"),sQuery(id+"F0.wireOp",EDGE,"E14.23.0"),sQuery(id+"F0.wireOp",EDGE,"E14.23.1"),sQuery(id+"F0.wireOp",EDGE,"E14.23.2"),sQuery(id+"F0.wireOp",EDGE,"E14.23.3"),sQuery(id+"F0.wireOp",EDGE,"E14.23.4"),sQuery(id+"F0.wireOp",EDGE,"E14.23.5"),sQuery(id+"F0.wireOp",EDGE,"E14.23.6"),sQuery(id+"F0.wireOp",EDGE,"E14.23.7"),sQuery(id+"F0.wireOp",EDGE,"E14.23.8"),sQuery(id+"F0.wireOp",EDGE,"E14.23.9"),sQuery(id+"F0.wireOp",EDGE,"E14.23.10"),sQuery(id+"F0.wireOp",EDGE,"E14.23.11"),sQuery(id+"F0.wireOp",EDGE,"E15.trimOffspring"),sQuery(id+"F0.wireOp",EDGE,"E16.trimOffspring"),sQuery(id+"F0.wireOp",EDGE,"E17.trimOffspring"),sQuery(id+"F0.wireOp",EDGE,"E18.trimOffspring"),sQuery(id+"F0.wireOp",EDGE,"E19.trimOffspring"),sQuery(id+"F0.wireOp",EDGE,"E20.trimOffspring"),sQuery(id+"F0.wireOp",EDGE,"E21.trimOffspring"),sQuery(id+"F0.wireOp",EDGE,"E22.trimOffspring"),sQuery(id+"F0.wireOp",EDGE,"E23.trimOffspring"),sQuery(id+"F0.wireOp",EDGE,"E24.trimOffspring"),sQuery(id+"F0.wireOp",EDGE,"E25.trimOffspring"),sQuery(id+"F0.wireOp",EDGE,"E26.trimOffspring"),sQuery(id+"F0.wireOp",EDGE,"E27.trimOffspring"),sQuery(id+"F0.wireOp",EDGE,"E28.trimOffspring"),sQuery(id+"F0.wireOp",EDGE,"E29.trimOffspring"),sQuery(id+"F0.wireOp",EDGE,"E30.trimOffspring"),sQuery(id+"F0.wireOp",EDGE,"E31.trimOffspring"),sQuery(id+"F0.wireOp",EDGE,"E32.trimOffspring"),sQuery(id+"F0.wireOp",EDGE,"E33.trimOffspring"),sQuery(id+"F0.wireOp",EDGE,"E34.trimOffspring"),sQuery(id+"F0.wireOp",EDGE,"E35.trimOffspring"),sQuery(id+"F0.wireOp",EDGE,"E36.trimOffspring"),sQuery(id+"F0.wireOp",EDGE,"E37.trimOffspring")])],"isStart":true});
            var sketch = newSketch(context, id + "F4", { "sketchPlane" : qUnion([Q0])});
            skCircle(sketch, "E39", {"center": v(0, 0) * mm, "radius": 6.35 * mm});
            skSolve(sketch);
        }
        {
            var Q0;
            Q0 = qSketchRegion(id + "F4", true);
            extrude(context, id + "F5", {"entities" : qUnion([Q0]), "operationType" : NewBodyOperationType.REMOVE, "oppositeDirection" : true, "depth" : 6.35 * mm});
        }
    });
